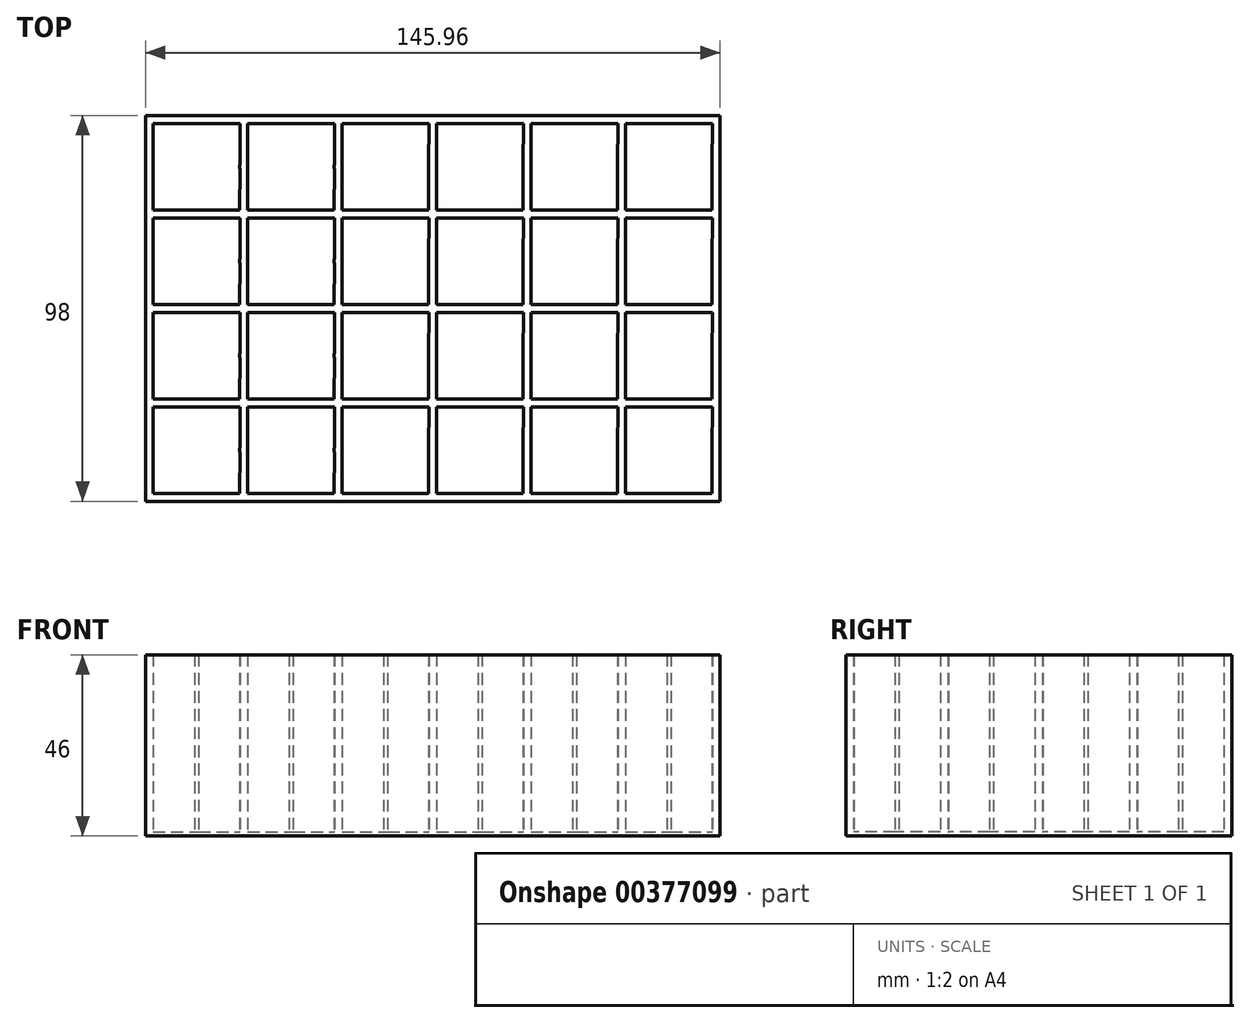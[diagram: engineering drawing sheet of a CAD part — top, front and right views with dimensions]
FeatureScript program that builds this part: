
annotation { "Feature Type Name" : "Feature", "Feature Type Description" : "" }
export const myFeature = defineFeature(function(context is Context, id is Id, definition is map)
    precondition{}
    {
        {
            var Q0;
            Q0=qCreatedBy(makeId("Top.planeOp"),FACE);
            var sketch = newSketch(context, id + "F0", { "sketchPlane" : qUnion([Q0])});
            skLineSegment(sketch, "E0.bottom", {"start": v(-21.96, 22.04) * mm, "end": v(-11.46, 22.02) * mm});
            skLineSegment(sketch, "E0.top", {"start": v(-22, 0.04) * mm, "end": v(-11.46, 0.02) * mm});
            skLineSegment(sketch, "E0.left", {"start": v(-21.96, 22.04) * mm, "end": v(-21.98, 11.54) * mm});
            skLineSegment(sketch, "E0.right", {"start": v(0.04, 22) * mm, "end": v(0.02, 11.54) * mm});
            skLineSegment(sketch, "E1.top", {"start": v(-11.46, 22) * mm, "end": v(-10.46, 22) * mm});
            skLineSegment(sketch, "E1.left", {"start": v(-11.46, 22.02) * mm, "end": v(-11.46, 22) * mm});
            skLineSegment(sketch, "E1.right", {"start": v(-10.46, 22.02) * mm, "end": v(-10.46, 22) * mm});
            skLineSegment(sketch, "E2.bottom", {"start": v(-21.98, 11.54) * mm, "end": v(-21.96, 11.54) * mm});
            skLineSegment(sketch, "E2.top", {"start": v(-21.98, 10.54) * mm, "end": v(-21.96, 10.54) * mm});
            skLineSegment(sketch, "E2.right", {"start": v(-21.96, 11.54) * mm, "end": v(-21.96, 10.54) * mm});
            skLineSegment(sketch, "E3.bottom", {"start": v(0.02, 11.54) * mm, "end": v(0, 11.54) * mm});
            skLineSegment(sketch, "E3.top", {"start": v(0.02, 10.54) * mm, "end": v(0, 10.54) * mm});
            skLineSegment(sketch, "E3.right", {"start": v(0, 11.54) * mm, "end": v(0, 10.54) * mm});
            skLineSegment(sketch, "E4.top", {"start": v(-11.46, 0.04) * mm, "end": v(-10.46, 0.04) * mm});
            skLineSegment(sketch, "E4.left", {"start": v(-11.46, 0.02) * mm, "end": v(-11.46, 0.04) * mm});
            skLineSegment(sketch, "E4.right", {"start": v(-10.46, 0.02) * mm, "end": v(-10.46, 0.04) * mm});
            skLineSegment(sketch, "E5.trimOffspring", {"start": v(-10.46, 22.02) * mm, "end": v(0.04, 22) * mm});
            skLineSegment(sketch, "E6.trimOffspring", {"start": v(-21.98, 10.54) * mm, "end": v(-22, 0.04) * mm});
            skLineSegment(sketch, "E7.trimOffspring", {"start": v(0.02, 10.54) * mm, "end": v(0, 0) * mm});
            skLineSegment(sketch, "E8.trimOffspring", {"start": v(-10.46, 0.02) * mm, "end": v(0, 0) * mm});
            skLineSegment(sketch, "E9.0.1.0", {"start": v(0.04, 46) * mm, "end": v(0.02, 35.54) * mm});
            skLineSegment(sketch, "E9.0.1.1", {"start": v(0.02, 34.54) * mm, "end": v(0, 24) * mm});
            skLineSegment(sketch, "E9.0.1.2", {"start": v(-21.96, 46.04) * mm, "end": v(-21.98, 35.54) * mm});
            skLineSegment(sketch, "E9.0.1.3", {"start": v(-22, 24.04) * mm, "end": v(-11.46, 24.02) * mm});
            skLineSegment(sketch, "E9.0.1.4", {"start": v(-21.96, 46.04) * mm, "end": v(-11.46, 46.02) * mm});
            skLineSegment(sketch, "E9.0.1.5", {"start": v(-10.46, 46.02) * mm, "end": v(0.04, 46) * mm});
            skLineSegment(sketch, "E9.0.1.6", {"start": v(-21.98, 34.54) * mm, "end": v(-22, 24.04) * mm});
            skLineSegment(sketch, "E9.0.1.7", {"start": v(-10.46, 24.02) * mm, "end": v(0, 24) * mm});
            skLineSegment(sketch, "E9.0.1.8", {"start": v(-11.46, 46.02) * mm, "end": v(-11.46, 46) * mm});
            skLineSegment(sketch, "E9.0.1.9", {"start": v(-11.46, 46) * mm, "end": v(-10.46, 46) * mm});
            skLineSegment(sketch, "E9.0.1.10", {"start": v(-10.46, 46.02) * mm, "end": v(-10.46, 46) * mm});
            skLineSegment(sketch, "E9.0.1.11", {"start": v(-21.96, 35.54) * mm, "end": v(-21.96, 34.54) * mm});
            skLineSegment(sketch, "E9.0.1.12", {"start": v(-21.98, 35.54) * mm, "end": v(-21.96, 35.54) * mm});
            skLineSegment(sketch, "E9.0.1.13", {"start": v(-21.98, 34.54) * mm, "end": v(-21.96, 34.54) * mm});
            skLineSegment(sketch, "E9.0.1.14", {"start": v(0.02, 34.54) * mm, "end": v(0, 34.54) * mm});
            skLineSegment(sketch, "E9.0.1.15", {"start": v(0.02, 35.54) * mm, "end": v(0, 35.54) * mm});
            skLineSegment(sketch, "E9.0.1.16", {"start": v(0, 35.54) * mm, "end": v(0, 34.54) * mm});
            skLineSegment(sketch, "E9.0.1.17", {"start": v(-10.46, 24.02) * mm, "end": v(-10.46, 24.04) * mm});
            skLineSegment(sketch, "E9.0.1.18", {"start": v(-11.46, 24.02) * mm, "end": v(-11.46, 24.04) * mm});
            skLineSegment(sketch, "E9.0.1.19", {"start": v(-11.46, 24.04) * mm, "end": v(-10.46, 24.04) * mm});
            skLineSegment(sketch, "E9.0.2.0", {"start": v(0.04, 70) * mm, "end": v(0.02, 59.54) * mm});
            skLineSegment(sketch, "E9.0.2.1", {"start": v(0.02, 58.54) * mm, "end": v(0, 48) * mm});
            skLineSegment(sketch, "E9.0.2.2", {"start": v(-21.96, 70.04) * mm, "end": v(-21.98, 59.54) * mm});
            skLineSegment(sketch, "E9.0.2.3", {"start": v(-22, 48.04) * mm, "end": v(-11.46, 48.02) * mm});
            skLineSegment(sketch, "E9.0.2.4", {"start": v(-21.96, 70.04) * mm, "end": v(-11.46, 70.02) * mm});
            skLineSegment(sketch, "E9.0.2.5", {"start": v(-10.46, 70.02) * mm, "end": v(0.04, 70) * mm});
            skLineSegment(sketch, "E9.0.2.6", {"start": v(-21.98, 58.54) * mm, "end": v(-22, 48.04) * mm});
            skLineSegment(sketch, "E9.0.2.7", {"start": v(-10.46, 48.02) * mm, "end": v(0, 48) * mm});
            skLineSegment(sketch, "E9.0.2.8", {"start": v(-11.46, 70.02) * mm, "end": v(-11.46, 70) * mm});
            skLineSegment(sketch, "E9.0.2.9", {"start": v(-11.46, 70) * mm, "end": v(-10.46, 70) * mm});
            skLineSegment(sketch, "E9.0.2.10", {"start": v(-10.46, 70.02) * mm, "end": v(-10.46, 70) * mm});
            skLineSegment(sketch, "E9.0.2.11", {"start": v(-21.96, 59.54) * mm, "end": v(-21.96, 58.54) * mm});
            skLineSegment(sketch, "E9.0.2.12", {"start": v(-21.98, 59.54) * mm, "end": v(-21.96, 59.54) * mm});
            skLineSegment(sketch, "E9.0.2.13", {"start": v(-21.98, 58.54) * mm, "end": v(-21.96, 58.54) * mm});
            skLineSegment(sketch, "E9.0.2.14", {"start": v(0.02, 58.54) * mm, "end": v(0, 58.54) * mm});
            skLineSegment(sketch, "E9.0.2.15", {"start": v(0.02, 59.54) * mm, "end": v(0, 59.54) * mm});
            skLineSegment(sketch, "E9.0.2.16", {"start": v(0, 59.54) * mm, "end": v(0, 58.54) * mm});
            skLineSegment(sketch, "E9.0.2.17", {"start": v(-10.46, 48.02) * mm, "end": v(-10.46, 48.04) * mm});
            skLineSegment(sketch, "E9.0.2.18", {"start": v(-11.46, 48.02) * mm, "end": v(-11.46, 48.04) * mm});
            skLineSegment(sketch, "E9.0.2.19", {"start": v(-11.46, 48.04) * mm, "end": v(-10.46, 48.04) * mm});
            skLineSegment(sketch, "E9.0.3.0", {"start": v(0.04, 94) * mm, "end": v(0.02, 83.54) * mm});
            skLineSegment(sketch, "E9.0.3.1", {"start": v(0.02, 82.54) * mm, "end": v(0, 72) * mm});
            skLineSegment(sketch, "E9.0.3.2", {"start": v(-21.96, 94.04) * mm, "end": v(-21.98, 83.54) * mm});
            skLineSegment(sketch, "E9.0.3.3", {"start": v(-22, 72.04) * mm, "end": v(-11.46, 72.02) * mm});
            skLineSegment(sketch, "E9.0.3.4", {"start": v(-21.96, 94.04) * mm, "end": v(-11.46, 94.02) * mm});
            skLineSegment(sketch, "E9.0.3.5", {"start": v(-10.46, 94.02) * mm, "end": v(0.04, 94) * mm});
            skLineSegment(sketch, "E9.0.3.6", {"start": v(-21.98, 82.54) * mm, "end": v(-22, 72.04) * mm});
            skLineSegment(sketch, "E9.0.3.7", {"start": v(-10.46, 72.02) * mm, "end": v(0, 72) * mm});
            skLineSegment(sketch, "E9.0.3.8", {"start": v(-11.46, 94.02) * mm, "end": v(-11.46, 94) * mm});
            skLineSegment(sketch, "E9.0.3.9", {"start": v(-11.46, 94) * mm, "end": v(-10.46, 94) * mm});
            skLineSegment(sketch, "E9.0.3.10", {"start": v(-10.46, 94.02) * mm, "end": v(-10.46, 94) * mm});
            skLineSegment(sketch, "E9.0.3.11", {"start": v(-21.96, 83.54) * mm, "end": v(-21.96, 82.54) * mm});
            skLineSegment(sketch, "E9.0.3.12", {"start": v(-21.98, 83.54) * mm, "end": v(-21.96, 83.54) * mm});
            skLineSegment(sketch, "E9.0.3.13", {"start": v(-21.98, 82.54) * mm, "end": v(-21.96, 82.54) * mm});
            skLineSegment(sketch, "E9.0.3.14", {"start": v(0.02, 82.54) * mm, "end": v(0, 82.54) * mm});
            skLineSegment(sketch, "E9.0.3.15", {"start": v(0.02, 83.54) * mm, "end": v(0, 83.54) * mm});
            skLineSegment(sketch, "E9.0.3.16", {"start": v(0, 83.54) * mm, "end": v(0, 82.54) * mm});
            skLineSegment(sketch, "E9.0.3.17", {"start": v(-10.46, 72.02) * mm, "end": v(-10.46, 72.04) * mm});
            skLineSegment(sketch, "E9.0.3.18", {"start": v(-11.46, 72.02) * mm, "end": v(-11.46, 72.04) * mm});
            skLineSegment(sketch, "E9.0.3.19", {"start": v(-11.46, 72.04) * mm, "end": v(-10.46, 72.04) * mm});
            skLineSegment(sketch, "E9.1.0.0", {"start": v(24.04, 22) * mm, "end": v(24.02, 11.54) * mm});
            skLineSegment(sketch, "E9.1.0.1", {"start": v(24.02, 10.54) * mm, "end": v(24, 0) * mm});
            skLineSegment(sketch, "E9.1.0.2", {"start": v(2.04, 22.04) * mm, "end": v(2.02, 11.54) * mm});
            skLineSegment(sketch, "E9.1.0.3", {"start": v(2, 0.04) * mm, "end": v(12.54, 0.02) * mm});
            skLineSegment(sketch, "E9.1.0.4", {"start": v(2.04, 22.04) * mm, "end": v(12.54, 22.02) * mm});
            skLineSegment(sketch, "E9.1.0.5", {"start": v(13.54, 22.02) * mm, "end": v(24.04, 22) * mm});
            skLineSegment(sketch, "E9.1.0.6", {"start": v(2.02, 10.54) * mm, "end": v(2, 0.04) * mm});
            skLineSegment(sketch, "E9.1.0.7", {"start": v(13.54, 0.02) * mm, "end": v(24, 0) * mm});
            skLineSegment(sketch, "E9.1.0.8", {"start": v(12.54, 22.02) * mm, "end": v(12.54, 22) * mm});
            skLineSegment(sketch, "E9.1.0.9", {"start": v(12.54, 22) * mm, "end": v(13.54, 22) * mm});
            skLineSegment(sketch, "E9.1.0.10", {"start": v(13.54, 22.02) * mm, "end": v(13.54, 22) * mm});
            skLineSegment(sketch, "E9.1.0.11", {"start": v(2.04, 11.54) * mm, "end": v(2.04, 10.54) * mm});
            skLineSegment(sketch, "E9.1.0.12", {"start": v(2.02, 11.54) * mm, "end": v(2.04, 11.54) * mm});
            skLineSegment(sketch, "E9.1.0.13", {"start": v(2.02, 10.54) * mm, "end": v(2.04, 10.54) * mm});
            skLineSegment(sketch, "E9.1.0.14", {"start": v(24.02, 10.54) * mm, "end": v(24, 10.54) * mm});
            skLineSegment(sketch, "E9.1.0.15", {"start": v(24.02, 11.54) * mm, "end": v(24, 11.54) * mm});
            skLineSegment(sketch, "E9.1.0.16", {"start": v(24, 11.54) * mm, "end": v(24, 10.54) * mm});
            skLineSegment(sketch, "E9.1.0.17", {"start": v(13.54, 0.02) * mm, "end": v(13.54, 0.04) * mm});
            skLineSegment(sketch, "E9.1.0.18", {"start": v(12.54, 0.02) * mm, "end": v(12.54, 0.04) * mm});
            skLineSegment(sketch, "E9.1.0.19", {"start": v(12.54, 0.04) * mm, "end": v(13.54, 0.04) * mm});
            skLineSegment(sketch, "E9.1.1.0", {"start": v(24.04, 46) * mm, "end": v(24.02, 35.54) * mm});
            skLineSegment(sketch, "E9.1.1.1", {"start": v(24.02, 34.54) * mm, "end": v(24, 24) * mm});
            skLineSegment(sketch, "E9.1.1.2", {"start": v(2.04, 46.04) * mm, "end": v(2.02, 35.54) * mm});
            skLineSegment(sketch, "E9.1.1.3", {"start": v(2, 24.04) * mm, "end": v(12.54, 24.02) * mm});
            skLineSegment(sketch, "E9.1.1.4", {"start": v(2.04, 46.04) * mm, "end": v(12.54, 46.02) * mm});
            skLineSegment(sketch, "E9.1.1.5", {"start": v(13.54, 46.02) * mm, "end": v(24.04, 46) * mm});
            skLineSegment(sketch, "E9.1.1.6", {"start": v(2.02, 34.54) * mm, "end": v(2, 24.04) * mm});
            skLineSegment(sketch, "E9.1.1.7", {"start": v(13.54, 24.02) * mm, "end": v(24, 24) * mm});
            skLineSegment(sketch, "E9.1.1.8", {"start": v(12.54, 46.02) * mm, "end": v(12.54, 46) * mm});
            skLineSegment(sketch, "E9.1.1.9", {"start": v(12.54, 46) * mm, "end": v(13.54, 46) * mm});
            skLineSegment(sketch, "E9.1.1.10", {"start": v(13.54, 46.02) * mm, "end": v(13.54, 46) * mm});
            skLineSegment(sketch, "E9.1.1.11", {"start": v(2.04, 35.54) * mm, "end": v(2.04, 34.54) * mm});
            skLineSegment(sketch, "E9.1.1.12", {"start": v(2.02, 35.54) * mm, "end": v(2.04, 35.54) * mm});
            skLineSegment(sketch, "E9.1.1.13", {"start": v(2.02, 34.54) * mm, "end": v(2.04, 34.54) * mm});
            skLineSegment(sketch, "E9.1.1.14", {"start": v(24.02, 34.54) * mm, "end": v(24, 34.54) * mm});
            skLineSegment(sketch, "E9.1.1.15", {"start": v(24.02, 35.54) * mm, "end": v(24, 35.54) * mm});
            skLineSegment(sketch, "E9.1.1.16", {"start": v(24, 35.54) * mm, "end": v(24, 34.54) * mm});
            skLineSegment(sketch, "E9.1.1.17", {"start": v(13.54, 24.02) * mm, "end": v(13.54, 24.04) * mm});
            skLineSegment(sketch, "E9.1.1.18", {"start": v(12.54, 24.02) * mm, "end": v(12.54, 24.04) * mm});
            skLineSegment(sketch, "E9.1.1.19", {"start": v(12.54, 24.04) * mm, "end": v(13.54, 24.04) * mm});
            skLineSegment(sketch, "E9.1.2.0", {"start": v(24.04, 70) * mm, "end": v(24.02, 59.54) * mm});
            skLineSegment(sketch, "E9.1.2.1", {"start": v(24.02, 58.54) * mm, "end": v(24, 48) * mm});
            skLineSegment(sketch, "E9.1.2.2", {"start": v(2.04, 70.04) * mm, "end": v(2.02, 59.54) * mm});
            skLineSegment(sketch, "E9.1.2.3", {"start": v(2, 48.04) * mm, "end": v(12.54, 48.02) * mm});
            skLineSegment(sketch, "E9.1.2.4", {"start": v(2.04, 70.04) * mm, "end": v(12.54, 70.02) * mm});
            skLineSegment(sketch, "E9.1.2.5", {"start": v(13.54, 70.02) * mm, "end": v(24.04, 70) * mm});
            skLineSegment(sketch, "E9.1.2.6", {"start": v(2.02, 58.54) * mm, "end": v(2, 48.04) * mm});
            skLineSegment(sketch, "E9.1.2.7", {"start": v(13.54, 48.02) * mm, "end": v(24, 48) * mm});
            skLineSegment(sketch, "E9.1.2.8", {"start": v(12.54, 70.02) * mm, "end": v(12.54, 70) * mm});
            skLineSegment(sketch, "E9.1.2.9", {"start": v(12.54, 70) * mm, "end": v(13.54, 70) * mm});
            skLineSegment(sketch, "E9.1.2.10", {"start": v(13.54, 70.02) * mm, "end": v(13.54, 70) * mm});
            skLineSegment(sketch, "E9.1.2.11", {"start": v(2.04, 59.54) * mm, "end": v(2.04, 58.54) * mm});
            skLineSegment(sketch, "E9.1.2.12", {"start": v(2.02, 59.54) * mm, "end": v(2.04, 59.54) * mm});
            skLineSegment(sketch, "E9.1.2.13", {"start": v(2.02, 58.54) * mm, "end": v(2.04, 58.54) * mm});
            skLineSegment(sketch, "E9.1.2.14", {"start": v(24.02, 58.54) * mm, "end": v(24, 58.54) * mm});
            skLineSegment(sketch, "E9.1.2.15", {"start": v(24.02, 59.54) * mm, "end": v(24, 59.54) * mm});
            skLineSegment(sketch, "E9.1.2.16", {"start": v(24, 59.54) * mm, "end": v(24, 58.54) * mm});
            skLineSegment(sketch, "E9.1.2.17", {"start": v(13.54, 48.02) * mm, "end": v(13.54, 48.04) * mm});
            skLineSegment(sketch, "E9.1.2.18", {"start": v(12.54, 48.02) * mm, "end": v(12.54, 48.04) * mm});
            skLineSegment(sketch, "E9.1.2.19", {"start": v(12.54, 48.04) * mm, "end": v(13.54, 48.04) * mm});
            skLineSegment(sketch, "E9.1.3.0", {"start": v(24.04, 94) * mm, "end": v(24.02, 83.54) * mm});
            skLineSegment(sketch, "E9.1.3.1", {"start": v(24.02, 82.54) * mm, "end": v(24, 72) * mm});
            skLineSegment(sketch, "E9.1.3.2", {"start": v(2.04, 94.04) * mm, "end": v(2.02, 83.54) * mm});
            skLineSegment(sketch, "E9.1.3.3", {"start": v(2, 72.04) * mm, "end": v(12.54, 72.02) * mm});
            skLineSegment(sketch, "E9.1.3.4", {"start": v(2.04, 94.04) * mm, "end": v(12.54, 94.02) * mm});
            skLineSegment(sketch, "E9.1.3.5", {"start": v(13.54, 94.02) * mm, "end": v(24.04, 94) * mm});
            skLineSegment(sketch, "E9.1.3.6", {"start": v(2.02, 82.54) * mm, "end": v(2, 72.04) * mm});
            skLineSegment(sketch, "E9.1.3.7", {"start": v(13.54, 72.02) * mm, "end": v(24, 72) * mm});
            skLineSegment(sketch, "E9.1.3.8", {"start": v(12.54, 94.02) * mm, "end": v(12.54, 94) * mm});
            skLineSegment(sketch, "E9.1.3.9", {"start": v(12.54, 94) * mm, "end": v(13.54, 94) * mm});
            skLineSegment(sketch, "E9.1.3.10", {"start": v(13.54, 94.02) * mm, "end": v(13.54, 94) * mm});
            skLineSegment(sketch, "E9.1.3.11", {"start": v(2.04, 83.54) * mm, "end": v(2.04, 82.54) * mm});
            skLineSegment(sketch, "E9.1.3.12", {"start": v(2.02, 83.54) * mm, "end": v(2.04, 83.54) * mm});
            skLineSegment(sketch, "E9.1.3.13", {"start": v(2.02, 82.54) * mm, "end": v(2.04, 82.54) * mm});
            skLineSegment(sketch, "E9.1.3.14", {"start": v(24.02, 82.54) * mm, "end": v(24, 82.54) * mm});
            skLineSegment(sketch, "E9.1.3.15", {"start": v(24.02, 83.54) * mm, "end": v(24, 83.54) * mm});
            skLineSegment(sketch, "E9.1.3.16", {"start": v(24, 83.54) * mm, "end": v(24, 82.54) * mm});
            skLineSegment(sketch, "E9.1.3.17", {"start": v(13.54, 72.02) * mm, "end": v(13.54, 72.04) * mm});
            skLineSegment(sketch, "E9.1.3.18", {"start": v(12.54, 72.02) * mm, "end": v(12.54, 72.04) * mm});
            skLineSegment(sketch, "E9.1.3.19", {"start": v(12.54, 72.04) * mm, "end": v(13.54, 72.04) * mm});
            skLineSegment(sketch, "E9.2.0.0", {"start": v(48.04, 22) * mm, "end": v(48.02, 11.54) * mm});
            skLineSegment(sketch, "E9.2.0.1", {"start": v(48.02, 10.54) * mm, "end": v(48, 0) * mm});
            skLineSegment(sketch, "E9.2.0.2", {"start": v(26.04, 22.04) * mm, "end": v(26.02, 11.54) * mm});
            skLineSegment(sketch, "E9.2.0.3", {"start": v(26, 0.04) * mm, "end": v(36.54, 0.02) * mm});
            skLineSegment(sketch, "E9.2.0.4", {"start": v(26.04, 22.04) * mm, "end": v(36.54, 22.02) * mm});
            skLineSegment(sketch, "E9.2.0.5", {"start": v(37.54, 22.02) * mm, "end": v(48.04, 22) * mm});
            skLineSegment(sketch, "E9.2.0.6", {"start": v(26.02, 10.54) * mm, "end": v(26, 0.04) * mm});
            skLineSegment(sketch, "E9.2.0.7", {"start": v(37.54, 0.02) * mm, "end": v(48, 0) * mm});
            skLineSegment(sketch, "E9.2.0.8", {"start": v(36.54, 22.02) * mm, "end": v(36.54, 22) * mm});
            skLineSegment(sketch, "E9.2.0.9", {"start": v(36.54, 22) * mm, "end": v(37.54, 22) * mm});
            skLineSegment(sketch, "E9.2.0.10", {"start": v(37.54, 22.02) * mm, "end": v(37.54, 22) * mm});
            skLineSegment(sketch, "E9.2.0.11", {"start": v(26.04, 11.54) * mm, "end": v(26.04, 10.54) * mm});
            skLineSegment(sketch, "E9.2.0.12", {"start": v(26.02, 11.54) * mm, "end": v(26.04, 11.54) * mm});
            skLineSegment(sketch, "E9.2.0.13", {"start": v(26.02, 10.54) * mm, "end": v(26.04, 10.54) * mm});
            skLineSegment(sketch, "E9.2.0.14", {"start": v(48.02, 10.54) * mm, "end": v(48, 10.54) * mm});
            skLineSegment(sketch, "E9.2.0.15", {"start": v(48.02, 11.54) * mm, "end": v(48, 11.54) * mm});
            skLineSegment(sketch, "E9.2.0.16", {"start": v(48, 11.54) * mm, "end": v(48, 10.54) * mm});
            skLineSegment(sketch, "E9.2.0.17", {"start": v(37.54, 0.02) * mm, "end": v(37.54, 0.04) * mm});
            skLineSegment(sketch, "E9.2.0.18", {"start": v(36.54, 0.02) * mm, "end": v(36.54, 0.04) * mm});
            skLineSegment(sketch, "E9.2.0.19", {"start": v(36.54, 0.04) * mm, "end": v(37.54, 0.04) * mm});
            skLineSegment(sketch, "E9.2.1.0", {"start": v(48.04, 46) * mm, "end": v(48.02, 35.54) * mm});
            skLineSegment(sketch, "E9.2.1.1", {"start": v(48.02, 34.54) * mm, "end": v(48, 24) * mm});
            skLineSegment(sketch, "E9.2.1.2", {"start": v(26.04, 46.04) * mm, "end": v(26.02, 35.54) * mm});
            skLineSegment(sketch, "E9.2.1.3", {"start": v(26, 24.04) * mm, "end": v(36.54, 24.02) * mm});
            skLineSegment(sketch, "E9.2.1.4", {"start": v(26.04, 46.04) * mm, "end": v(36.54, 46.02) * mm});
            skLineSegment(sketch, "E9.2.1.5", {"start": v(37.54, 46.02) * mm, "end": v(48.04, 46) * mm});
            skLineSegment(sketch, "E9.2.1.6", {"start": v(26.02, 34.54) * mm, "end": v(26, 24.04) * mm});
            skLineSegment(sketch, "E9.2.1.7", {"start": v(37.54, 24.02) * mm, "end": v(48, 24) * mm});
            skLineSegment(sketch, "E9.2.1.8", {"start": v(36.54, 46.02) * mm, "end": v(36.54, 46) * mm});
            skLineSegment(sketch, "E9.2.1.9", {"start": v(36.54, 46) * mm, "end": v(37.54, 46) * mm});
            skLineSegment(sketch, "E9.2.1.10", {"start": v(37.54, 46.02) * mm, "end": v(37.54, 46) * mm});
            skLineSegment(sketch, "E9.2.1.11", {"start": v(26.04, 35.54) * mm, "end": v(26.04, 34.54) * mm});
            skLineSegment(sketch, "E9.2.1.12", {"start": v(26.02, 35.54) * mm, "end": v(26.04, 35.54) * mm});
            skLineSegment(sketch, "E9.2.1.13", {"start": v(26.02, 34.54) * mm, "end": v(26.04, 34.54) * mm});
            skLineSegment(sketch, "E9.2.1.14", {"start": v(48.02, 34.54) * mm, "end": v(48, 34.54) * mm});
            skLineSegment(sketch, "E9.2.1.15", {"start": v(48.02, 35.54) * mm, "end": v(48, 35.54) * mm});
            skLineSegment(sketch, "E9.2.1.16", {"start": v(48, 35.54) * mm, "end": v(48, 34.54) * mm});
            skLineSegment(sketch, "E9.2.1.17", {"start": v(37.54, 24.02) * mm, "end": v(37.54, 24.04) * mm});
            skLineSegment(sketch, "E9.2.1.18", {"start": v(36.54, 24.02) * mm, "end": v(36.54, 24.04) * mm});
            skLineSegment(sketch, "E9.2.1.19", {"start": v(36.54, 24.04) * mm, "end": v(37.54, 24.04) * mm});
            skLineSegment(sketch, "E9.2.2.0", {"start": v(48.04, 70) * mm, "end": v(48.02, 59.54) * mm});
            skLineSegment(sketch, "E9.2.2.1", {"start": v(48.02, 58.54) * mm, "end": v(48, 48) * mm});
            skLineSegment(sketch, "E9.2.2.2", {"start": v(26.04, 70.04) * mm, "end": v(26.02, 59.54) * mm});
            skLineSegment(sketch, "E9.2.2.3", {"start": v(26, 48.04) * mm, "end": v(36.54, 48.02) * mm});
            skLineSegment(sketch, "E9.2.2.4", {"start": v(26.04, 70.04) * mm, "end": v(36.54, 70.02) * mm});
            skLineSegment(sketch, "E9.2.2.5", {"start": v(37.54, 70.02) * mm, "end": v(48.04, 70) * mm});
            skLineSegment(sketch, "E9.2.2.6", {"start": v(26.02, 58.54) * mm, "end": v(26, 48.04) * mm});
            skLineSegment(sketch, "E9.2.2.7", {"start": v(37.54, 48.02) * mm, "end": v(48, 48) * mm});
            skLineSegment(sketch, "E9.2.2.8", {"start": v(36.54, 70.02) * mm, "end": v(36.54, 70) * mm});
            skLineSegment(sketch, "E9.2.2.9", {"start": v(36.54, 70) * mm, "end": v(37.54, 70) * mm});
            skLineSegment(sketch, "E9.2.2.10", {"start": v(37.54, 70.02) * mm, "end": v(37.54, 70) * mm});
            skLineSegment(sketch, "E9.2.2.11", {"start": v(26.04, 59.54) * mm, "end": v(26.04, 58.54) * mm});
            skLineSegment(sketch, "E9.2.2.12", {"start": v(26.02, 59.54) * mm, "end": v(26.04, 59.54) * mm});
            skLineSegment(sketch, "E9.2.2.13", {"start": v(26.02, 58.54) * mm, "end": v(26.04, 58.54) * mm});
            skLineSegment(sketch, "E9.2.2.14", {"start": v(48.02, 58.54) * mm, "end": v(48, 58.54) * mm});
            skLineSegment(sketch, "E9.2.2.15", {"start": v(48.02, 59.54) * mm, "end": v(48, 59.54) * mm});
            skLineSegment(sketch, "E9.2.2.16", {"start": v(48, 59.54) * mm, "end": v(48, 58.54) * mm});
            skLineSegment(sketch, "E9.2.2.17", {"start": v(37.54, 48.02) * mm, "end": v(37.54, 48.04) * mm});
            skLineSegment(sketch, "E9.2.2.18", {"start": v(36.54, 48.02) * mm, "end": v(36.54, 48.04) * mm});
            skLineSegment(sketch, "E9.2.2.19", {"start": v(36.54, 48.04) * mm, "end": v(37.54, 48.04) * mm});
            skLineSegment(sketch, "E9.2.3.0", {"start": v(48.04, 94) * mm, "end": v(48.02, 83.54) * mm});
            skLineSegment(sketch, "E9.2.3.1", {"start": v(48.02, 82.54) * mm, "end": v(48, 72) * mm});
            skLineSegment(sketch, "E9.2.3.2", {"start": v(26.04, 94.04) * mm, "end": v(26.02, 83.54) * mm});
            skLineSegment(sketch, "E9.2.3.3", {"start": v(26, 72.04) * mm, "end": v(36.54, 72.02) * mm});
            skLineSegment(sketch, "E9.2.3.4", {"start": v(26.04, 94.04) * mm, "end": v(36.54, 94.02) * mm});
            skLineSegment(sketch, "E9.2.3.5", {"start": v(37.54, 94.02) * mm, "end": v(48.04, 94) * mm});
            skLineSegment(sketch, "E9.2.3.6", {"start": v(26.02, 82.54) * mm, "end": v(26, 72.04) * mm});
            skLineSegment(sketch, "E9.2.3.7", {"start": v(37.54, 72.02) * mm, "end": v(48, 72) * mm});
            skLineSegment(sketch, "E9.2.3.8", {"start": v(36.54, 94.02) * mm, "end": v(36.54, 94) * mm});
            skLineSegment(sketch, "E9.2.3.9", {"start": v(36.54, 94) * mm, "end": v(37.54, 94) * mm});
            skLineSegment(sketch, "E9.2.3.10", {"start": v(37.54, 94.02) * mm, "end": v(37.54, 94) * mm});
            skLineSegment(sketch, "E9.2.3.11", {"start": v(26.04, 83.54) * mm, "end": v(26.04, 82.54) * mm});
            skLineSegment(sketch, "E9.2.3.12", {"start": v(26.02, 83.54) * mm, "end": v(26.04, 83.54) * mm});
            skLineSegment(sketch, "E9.2.3.13", {"start": v(26.02, 82.54) * mm, "end": v(26.04, 82.54) * mm});
            skLineSegment(sketch, "E9.2.3.14", {"start": v(48.02, 82.54) * mm, "end": v(48, 82.54) * mm});
            skLineSegment(sketch, "E9.2.3.15", {"start": v(48.02, 83.54) * mm, "end": v(48, 83.54) * mm});
            skLineSegment(sketch, "E9.2.3.16", {"start": v(48, 83.54) * mm, "end": v(48, 82.54) * mm});
            skLineSegment(sketch, "E9.2.3.17", {"start": v(37.54, 72.02) * mm, "end": v(37.54, 72.04) * mm});
            skLineSegment(sketch, "E9.2.3.18", {"start": v(36.54, 72.02) * mm, "end": v(36.54, 72.04) * mm});
            skLineSegment(sketch, "E9.2.3.19", {"start": v(36.54, 72.04) * mm, "end": v(37.54, 72.04) * mm});
            skLineSegment(sketch, "E9.3.0.0", {"start": v(72.04, 22) * mm, "end": v(72.02, 11.54) * mm});
            skLineSegment(sketch, "E9.3.0.1", {"start": v(72.02, 10.54) * mm, "end": v(72, 0) * mm});
            skLineSegment(sketch, "E9.3.0.2", {"start": v(50.04, 22.04) * mm, "end": v(50.02, 11.54) * mm});
            skLineSegment(sketch, "E9.3.0.3", {"start": v(50, 0.04) * mm, "end": v(60.54, 0.02) * mm});
            skLineSegment(sketch, "E9.3.0.4", {"start": v(50.04, 22.04) * mm, "end": v(60.54, 22.02) * mm});
            skLineSegment(sketch, "E9.3.0.5", {"start": v(61.54, 22.02) * mm, "end": v(72.04, 22) * mm});
            skLineSegment(sketch, "E9.3.0.6", {"start": v(50.02, 10.54) * mm, "end": v(50, 0.04) * mm});
            skLineSegment(sketch, "E9.3.0.7", {"start": v(61.54, 0.02) * mm, "end": v(72, 0) * mm});
            skLineSegment(sketch, "E9.3.0.8", {"start": v(60.54, 22.02) * mm, "end": v(60.54, 22) * mm});
            skLineSegment(sketch, "E9.3.0.9", {"start": v(60.54, 22) * mm, "end": v(61.54, 22) * mm});
            skLineSegment(sketch, "E9.3.0.10", {"start": v(61.54, 22.02) * mm, "end": v(61.54, 22) * mm});
            skLineSegment(sketch, "E9.3.0.11", {"start": v(50.04, 11.54) * mm, "end": v(50.04, 10.54) * mm});
            skLineSegment(sketch, "E9.3.0.12", {"start": v(50.02, 11.54) * mm, "end": v(50.04, 11.54) * mm});
            skLineSegment(sketch, "E9.3.0.13", {"start": v(50.02, 10.54) * mm, "end": v(50.04, 10.54) * mm});
            skLineSegment(sketch, "E9.3.0.14", {"start": v(72.02, 10.54) * mm, "end": v(72, 10.54) * mm});
            skLineSegment(sketch, "E9.3.0.15", {"start": v(72.02, 11.54) * mm, "end": v(72, 11.54) * mm});
            skLineSegment(sketch, "E9.3.0.16", {"start": v(72, 11.54) * mm, "end": v(72, 10.54) * mm});
            skLineSegment(sketch, "E9.3.0.17", {"start": v(61.54, 0.02) * mm, "end": v(61.54, 0.04) * mm});
            skLineSegment(sketch, "E9.3.0.18", {"start": v(60.54, 0.02) * mm, "end": v(60.54, 0.04) * mm});
            skLineSegment(sketch, "E9.3.0.19", {"start": v(60.54, 0.04) * mm, "end": v(61.54, 0.04) * mm});
            skLineSegment(sketch, "E9.3.1.0", {"start": v(72.04, 46) * mm, "end": v(72.02, 35.54) * mm});
            skLineSegment(sketch, "E9.3.1.1", {"start": v(72.02, 34.54) * mm, "end": v(72, 24) * mm});
            skLineSegment(sketch, "E9.3.1.2", {"start": v(50.04, 46.04) * mm, "end": v(50.02, 35.54) * mm});
            skLineSegment(sketch, "E9.3.1.3", {"start": v(50, 24.04) * mm, "end": v(60.54, 24.02) * mm});
            skLineSegment(sketch, "E9.3.1.4", {"start": v(50.04, 46.04) * mm, "end": v(60.54, 46.02) * mm});
            skLineSegment(sketch, "E9.3.1.5", {"start": v(61.54, 46.02) * mm, "end": v(72.04, 46) * mm});
            skLineSegment(sketch, "E9.3.1.6", {"start": v(50.02, 34.54) * mm, "end": v(50, 24.04) * mm});
            skLineSegment(sketch, "E9.3.1.7", {"start": v(61.54, 24.02) * mm, "end": v(72, 24) * mm});
            skLineSegment(sketch, "E9.3.1.8", {"start": v(60.54, 46.02) * mm, "end": v(60.54, 46) * mm});
            skLineSegment(sketch, "E9.3.1.9", {"start": v(60.54, 46) * mm, "end": v(61.54, 46) * mm});
            skLineSegment(sketch, "E9.3.1.10", {"start": v(61.54, 46.02) * mm, "end": v(61.54, 46) * mm});
            skLineSegment(sketch, "E9.3.1.11", {"start": v(50.04, 35.54) * mm, "end": v(50.04, 34.54) * mm});
            skLineSegment(sketch, "E9.3.1.12", {"start": v(50.02, 35.54) * mm, "end": v(50.04, 35.54) * mm});
            skLineSegment(sketch, "E9.3.1.13", {"start": v(50.02, 34.54) * mm, "end": v(50.04, 34.54) * mm});
            skLineSegment(sketch, "E9.3.1.14", {"start": v(72.02, 34.54) * mm, "end": v(72, 34.54) * mm});
            skLineSegment(sketch, "E9.3.1.15", {"start": v(72.02, 35.54) * mm, "end": v(72, 35.54) * mm});
            skLineSegment(sketch, "E9.3.1.16", {"start": v(72, 35.54) * mm, "end": v(72, 34.54) * mm});
            skLineSegment(sketch, "E9.3.1.17", {"start": v(61.54, 24.02) * mm, "end": v(61.54, 24.04) * mm});
            skLineSegment(sketch, "E9.3.1.18", {"start": v(60.54, 24.02) * mm, "end": v(60.54, 24.04) * mm});
            skLineSegment(sketch, "E9.3.1.19", {"start": v(60.54, 24.04) * mm, "end": v(61.54, 24.04) * mm});
            skLineSegment(sketch, "E9.3.2.0", {"start": v(72.04, 70) * mm, "end": v(72.02, 59.54) * mm});
            skLineSegment(sketch, "E9.3.2.1", {"start": v(72.02, 58.54) * mm, "end": v(72, 48) * mm});
            skLineSegment(sketch, "E9.3.2.2", {"start": v(50.04, 70.04) * mm, "end": v(50.02, 59.54) * mm});
            skLineSegment(sketch, "E9.3.2.3", {"start": v(50, 48.04) * mm, "end": v(60.54, 48.02) * mm});
            skLineSegment(sketch, "E9.3.2.4", {"start": v(50.04, 70.04) * mm, "end": v(60.54, 70.02) * mm});
            skLineSegment(sketch, "E9.3.2.5", {"start": v(61.54, 70.02) * mm, "end": v(72.04, 70) * mm});
            skLineSegment(sketch, "E9.3.2.6", {"start": v(50.02, 58.54) * mm, "end": v(50, 48.04) * mm});
            skLineSegment(sketch, "E9.3.2.7", {"start": v(61.54, 48.02) * mm, "end": v(72, 48) * mm});
            skLineSegment(sketch, "E9.3.2.8", {"start": v(60.54, 70.02) * mm, "end": v(60.54, 70) * mm});
            skLineSegment(sketch, "E9.3.2.9", {"start": v(60.54, 70) * mm, "end": v(61.54, 70) * mm});
            skLineSegment(sketch, "E9.3.2.10", {"start": v(61.54, 70.02) * mm, "end": v(61.54, 70) * mm});
            skLineSegment(sketch, "E9.3.2.11", {"start": v(50.04, 59.54) * mm, "end": v(50.04, 58.54) * mm});
            skLineSegment(sketch, "E9.3.2.12", {"start": v(50.02, 59.54) * mm, "end": v(50.04, 59.54) * mm});
            skLineSegment(sketch, "E9.3.2.13", {"start": v(50.02, 58.54) * mm, "end": v(50.04, 58.54) * mm});
            skLineSegment(sketch, "E9.3.2.14", {"start": v(72.02, 58.54) * mm, "end": v(72, 58.54) * mm});
            skLineSegment(sketch, "E9.3.2.15", {"start": v(72.02, 59.54) * mm, "end": v(72, 59.54) * mm});
            skLineSegment(sketch, "E9.3.2.16", {"start": v(72, 59.54) * mm, "end": v(72, 58.54) * mm});
            skLineSegment(sketch, "E9.3.2.17", {"start": v(61.54, 48.02) * mm, "end": v(61.54, 48.04) * mm});
            skLineSegment(sketch, "E9.3.2.18", {"start": v(60.54, 48.02) * mm, "end": v(60.54, 48.04) * mm});
            skLineSegment(sketch, "E9.3.2.19", {"start": v(60.54, 48.04) * mm, "end": v(61.54, 48.04) * mm});
            skLineSegment(sketch, "E9.3.3.0", {"start": v(72.04, 94) * mm, "end": v(72.02, 83.54) * mm});
            skLineSegment(sketch, "E9.3.3.1", {"start": v(72.02, 82.54) * mm, "end": v(72, 72) * mm});
            skLineSegment(sketch, "E9.3.3.2", {"start": v(50.04, 94.04) * mm, "end": v(50.02, 83.54) * mm});
            skLineSegment(sketch, "E9.3.3.3", {"start": v(50, 72.04) * mm, "end": v(60.54, 72.02) * mm});
            skLineSegment(sketch, "E9.3.3.4", {"start": v(50.04, 94.04) * mm, "end": v(60.54, 94.02) * mm});
            skLineSegment(sketch, "E9.3.3.5", {"start": v(61.54, 94.02) * mm, "end": v(72.04, 94) * mm});
            skLineSegment(sketch, "E9.3.3.6", {"start": v(50.02, 82.54) * mm, "end": v(50, 72.04) * mm});
            skLineSegment(sketch, "E9.3.3.7", {"start": v(61.54, 72.02) * mm, "end": v(72, 72) * mm});
            skLineSegment(sketch, "E9.3.3.8", {"start": v(60.54, 94.02) * mm, "end": v(60.54, 94) * mm});
            skLineSegment(sketch, "E9.3.3.9", {"start": v(60.54, 94) * mm, "end": v(61.54, 94) * mm});
            skLineSegment(sketch, "E9.3.3.10", {"start": v(61.54, 94.02) * mm, "end": v(61.54, 94) * mm});
            skLineSegment(sketch, "E9.3.3.11", {"start": v(50.04, 83.54) * mm, "end": v(50.04, 82.54) * mm});
            skLineSegment(sketch, "E9.3.3.12", {"start": v(50.02, 83.54) * mm, "end": v(50.04, 83.54) * mm});
            skLineSegment(sketch, "E9.3.3.13", {"start": v(50.02, 82.54) * mm, "end": v(50.04, 82.54) * mm});
            skLineSegment(sketch, "E9.3.3.14", {"start": v(72.02, 82.54) * mm, "end": v(72, 82.54) * mm});
            skLineSegment(sketch, "E9.3.3.15", {"start": v(72.02, 83.54) * mm, "end": v(72, 83.54) * mm});
            skLineSegment(sketch, "E9.3.3.16", {"start": v(72, 83.54) * mm, "end": v(72, 82.54) * mm});
            skLineSegment(sketch, "E9.3.3.17", {"start": v(61.54, 72.02) * mm, "end": v(61.54, 72.04) * mm});
            skLineSegment(sketch, "E9.3.3.18", {"start": v(60.54, 72.02) * mm, "end": v(60.54, 72.04) * mm});
            skLineSegment(sketch, "E9.3.3.19", {"start": v(60.54, 72.04) * mm, "end": v(61.54, 72.04) * mm});
            skLineSegment(sketch, "E9.4.0.0", {"start": v(96.04, 22) * mm, "end": v(96.02, 11.54) * mm});
            skLineSegment(sketch, "E9.4.0.1", {"start": v(96.02, 10.54) * mm, "end": v(96, 0) * mm});
            skLineSegment(sketch, "E9.4.0.2", {"start": v(74.04, 22.04) * mm, "end": v(74.02, 11.54) * mm});
            skLineSegment(sketch, "E9.4.0.3", {"start": v(74, 0.04) * mm, "end": v(84.54, 0.02) * mm});
            skLineSegment(sketch, "E9.4.0.4", {"start": v(74.04, 22.04) * mm, "end": v(84.54, 22.02) * mm});
            skLineSegment(sketch, "E9.4.0.5", {"start": v(85.54, 22.02) * mm, "end": v(96.04, 22) * mm});
            skLineSegment(sketch, "E9.4.0.6", {"start": v(74.02, 10.54) * mm, "end": v(74, 0.04) * mm});
            skLineSegment(sketch, "E9.4.0.7", {"start": v(85.54, 0.02) * mm, "end": v(96, 0) * mm});
            skLineSegment(sketch, "E9.4.0.8", {"start": v(84.54, 22.02) * mm, "end": v(84.54, 22) * mm});
            skLineSegment(sketch, "E9.4.0.9", {"start": v(84.54, 22) * mm, "end": v(85.54, 22) * mm});
            skLineSegment(sketch, "E9.4.0.10", {"start": v(85.54, 22.02) * mm, "end": v(85.54, 22) * mm});
            skLineSegment(sketch, "E9.4.0.11", {"start": v(74.04, 11.54) * mm, "end": v(74.04, 10.54) * mm});
            skLineSegment(sketch, "E9.4.0.12", {"start": v(74.02, 11.54) * mm, "end": v(74.04, 11.54) * mm});
            skLineSegment(sketch, "E9.4.0.13", {"start": v(74.02, 10.54) * mm, "end": v(74.04, 10.54) * mm});
            skLineSegment(sketch, "E9.4.0.14", {"start": v(96.02, 10.54) * mm, "end": v(96, 10.54) * mm});
            skLineSegment(sketch, "E9.4.0.15", {"start": v(96.02, 11.54) * mm, "end": v(96, 11.54) * mm});
            skLineSegment(sketch, "E9.4.0.16", {"start": v(96, 11.54) * mm, "end": v(96, 10.54) * mm});
            skLineSegment(sketch, "E9.4.0.17", {"start": v(85.54, 0.02) * mm, "end": v(85.54, 0.04) * mm});
            skLineSegment(sketch, "E9.4.0.18", {"start": v(84.54, 0.02) * mm, "end": v(84.54, 0.04) * mm});
            skLineSegment(sketch, "E9.4.0.19", {"start": v(84.54, 0.04) * mm, "end": v(85.54, 0.04) * mm});
            skLineSegment(sketch, "E9.4.1.0", {"start": v(96.04, 46) * mm, "end": v(96.02, 35.54) * mm});
            skLineSegment(sketch, "E9.4.1.1", {"start": v(96.02, 34.54) * mm, "end": v(96, 24) * mm});
            skLineSegment(sketch, "E9.4.1.2", {"start": v(74.04, 46.04) * mm, "end": v(74.02, 35.54) * mm});
            skLineSegment(sketch, "E9.4.1.3", {"start": v(74, 24.04) * mm, "end": v(84.54, 24.02) * mm});
            skLineSegment(sketch, "E9.4.1.4", {"start": v(74.04, 46.04) * mm, "end": v(84.54, 46.02) * mm});
            skLineSegment(sketch, "E9.4.1.5", {"start": v(85.54, 46.02) * mm, "end": v(96.04, 46) * mm});
            skLineSegment(sketch, "E9.4.1.6", {"start": v(74.02, 34.54) * mm, "end": v(74, 24.04) * mm});
            skLineSegment(sketch, "E9.4.1.7", {"start": v(85.54, 24.02) * mm, "end": v(96, 24) * mm});
            skLineSegment(sketch, "E9.4.1.8", {"start": v(84.54, 46.02) * mm, "end": v(84.54, 46) * mm});
            skLineSegment(sketch, "E9.4.1.9", {"start": v(84.54, 46) * mm, "end": v(85.54, 46) * mm});
            skLineSegment(sketch, "E9.4.1.10", {"start": v(85.54, 46.02) * mm, "end": v(85.54, 46) * mm});
            skLineSegment(sketch, "E9.4.1.11", {"start": v(74.04, 35.54) * mm, "end": v(74.04, 34.54) * mm});
            skLineSegment(sketch, "E9.4.1.12", {"start": v(74.02, 35.54) * mm, "end": v(74.04, 35.54) * mm});
            skLineSegment(sketch, "E9.4.1.13", {"start": v(74.02, 34.54) * mm, "end": v(74.04, 34.54) * mm});
            skLineSegment(sketch, "E9.4.1.14", {"start": v(96.02, 34.54) * mm, "end": v(96, 34.54) * mm});
            skLineSegment(sketch, "E9.4.1.15", {"start": v(96.02, 35.54) * mm, "end": v(96, 35.54) * mm});
            skLineSegment(sketch, "E9.4.1.16", {"start": v(96, 35.54) * mm, "end": v(96, 34.54) * mm});
            skLineSegment(sketch, "E9.4.1.17", {"start": v(85.54, 24.02) * mm, "end": v(85.54, 24.04) * mm});
            skLineSegment(sketch, "E9.4.1.18", {"start": v(84.54, 24.02) * mm, "end": v(84.54, 24.04) * mm});
            skLineSegment(sketch, "E9.4.1.19", {"start": v(84.54, 24.04) * mm, "end": v(85.54, 24.04) * mm});
            skLineSegment(sketch, "E9.4.2.0", {"start": v(96.04, 70) * mm, "end": v(96.02, 59.54) * mm});
            skLineSegment(sketch, "E9.4.2.1", {"start": v(96.02, 58.54) * mm, "end": v(96, 48) * mm});
            skLineSegment(sketch, "E9.4.2.2", {"start": v(74.04, 70.04) * mm, "end": v(74.02, 59.54) * mm});
            skLineSegment(sketch, "E9.4.2.3", {"start": v(74, 48.04) * mm, "end": v(84.54, 48.02) * mm});
            skLineSegment(sketch, "E9.4.2.4", {"start": v(74.04, 70.04) * mm, "end": v(84.54, 70.02) * mm});
            skLineSegment(sketch, "E9.4.2.5", {"start": v(85.54, 70.02) * mm, "end": v(96.04, 70) * mm});
            skLineSegment(sketch, "E9.4.2.6", {"start": v(74.02, 58.54) * mm, "end": v(74, 48.04) * mm});
            skLineSegment(sketch, "E9.4.2.7", {"start": v(85.54, 48.02) * mm, "end": v(96, 48) * mm});
            skLineSegment(sketch, "E9.4.2.8", {"start": v(84.54, 70.02) * mm, "end": v(84.54, 70) * mm});
            skLineSegment(sketch, "E9.4.2.9", {"start": v(84.54, 70) * mm, "end": v(85.54, 70) * mm});
            skLineSegment(sketch, "E9.4.2.10", {"start": v(85.54, 70.02) * mm, "end": v(85.54, 70) * mm});
            skLineSegment(sketch, "E9.4.2.11", {"start": v(74.04, 59.54) * mm, "end": v(74.04, 58.54) * mm});
            skLineSegment(sketch, "E9.4.2.12", {"start": v(74.02, 59.54) * mm, "end": v(74.04, 59.54) * mm});
            skLineSegment(sketch, "E9.4.2.13", {"start": v(74.02, 58.54) * mm, "end": v(74.04, 58.54) * mm});
            skLineSegment(sketch, "E9.4.2.14", {"start": v(96.02, 58.54) * mm, "end": v(96, 58.54) * mm});
            skLineSegment(sketch, "E9.4.2.15", {"start": v(96.02, 59.54) * mm, "end": v(96, 59.54) * mm});
            skLineSegment(sketch, "E9.4.2.16", {"start": v(96, 59.54) * mm, "end": v(96, 58.54) * mm});
            skLineSegment(sketch, "E9.4.2.17", {"start": v(85.54, 48.02) * mm, "end": v(85.54, 48.04) * mm});
            skLineSegment(sketch, "E9.4.2.18", {"start": v(84.54, 48.02) * mm, "end": v(84.54, 48.04) * mm});
            skLineSegment(sketch, "E9.4.2.19", {"start": v(84.54, 48.04) * mm, "end": v(85.54, 48.04) * mm});
            skLineSegment(sketch, "E9.4.3.0", {"start": v(96.04, 94) * mm, "end": v(96.02, 83.54) * mm});
            skLineSegment(sketch, "E9.4.3.1", {"start": v(96.02, 82.54) * mm, "end": v(96, 72) * mm});
            skLineSegment(sketch, "E9.4.3.2", {"start": v(74.04, 94.04) * mm, "end": v(74.02, 83.54) * mm});
            skLineSegment(sketch, "E9.4.3.3", {"start": v(74, 72.04) * mm, "end": v(84.54, 72.02) * mm});
            skLineSegment(sketch, "E9.4.3.4", {"start": v(74.04, 94.04) * mm, "end": v(84.54, 94.02) * mm});
            skLineSegment(sketch, "E9.4.3.5", {"start": v(85.54, 94.02) * mm, "end": v(96.04, 94) * mm});
            skLineSegment(sketch, "E9.4.3.6", {"start": v(74.02, 82.54) * mm, "end": v(74, 72.04) * mm});
            skLineSegment(sketch, "E9.4.3.7", {"start": v(85.54, 72.02) * mm, "end": v(96, 72) * mm});
            skLineSegment(sketch, "E9.4.3.8", {"start": v(84.54, 94.02) * mm, "end": v(84.54, 94) * mm});
            skLineSegment(sketch, "E9.4.3.9", {"start": v(84.54, 94) * mm, "end": v(85.54, 94) * mm});
            skLineSegment(sketch, "E9.4.3.10", {"start": v(85.54, 94.02) * mm, "end": v(85.54, 94) * mm});
            skLineSegment(sketch, "E9.4.3.11", {"start": v(74.04, 83.54) * mm, "end": v(74.04, 82.54) * mm});
            skLineSegment(sketch, "E9.4.3.12", {"start": v(74.02, 83.54) * mm, "end": v(74.04, 83.54) * mm});
            skLineSegment(sketch, "E9.4.3.13", {"start": v(74.02, 82.54) * mm, "end": v(74.04, 82.54) * mm});
            skLineSegment(sketch, "E9.4.3.14", {"start": v(96.02, 82.54) * mm, "end": v(96, 82.54) * mm});
            skLineSegment(sketch, "E9.4.3.15", {"start": v(96.02, 83.54) * mm, "end": v(96, 83.54) * mm});
            skLineSegment(sketch, "E9.4.3.16", {"start": v(96, 83.54) * mm, "end": v(96, 82.54) * mm});
            skLineSegment(sketch, "E9.4.3.17", {"start": v(85.54, 72.02) * mm, "end": v(85.54, 72.04) * mm});
            skLineSegment(sketch, "E9.4.3.18", {"start": v(84.54, 72.02) * mm, "end": v(84.54, 72.04) * mm});
            skLineSegment(sketch, "E9.4.3.19", {"start": v(84.54, 72.04) * mm, "end": v(85.54, 72.04) * mm});
            skLineSegment(sketch, "E9.5.0.0", {"start": v(120.04, 22) * mm, "end": v(120.02, 11.54) * mm});
            skLineSegment(sketch, "E9.5.0.1", {"start": v(120.02, 10.54) * mm, "end": v(120, 0) * mm});
            skLineSegment(sketch, "E9.5.0.2", {"start": v(98.04, 22.04) * mm, "end": v(98.02, 11.54) * mm});
            skLineSegment(sketch, "E9.5.0.3", {"start": v(98, 0.04) * mm, "end": v(108.54, 0.02) * mm});
            skLineSegment(sketch, "E9.5.0.4", {"start": v(98.04, 22.04) * mm, "end": v(108.54, 22.02) * mm});
            skLineSegment(sketch, "E9.5.0.5", {"start": v(109.54, 22.02) * mm, "end": v(120.04, 22) * mm});
            skLineSegment(sketch, "E9.5.0.6", {"start": v(98.02, 10.54) * mm, "end": v(98, 0.04) * mm});
            skLineSegment(sketch, "E9.5.0.7", {"start": v(109.54, 0.02) * mm, "end": v(120, 0) * mm});
            skLineSegment(sketch, "E9.5.0.8", {"start": v(108.54, 22.02) * mm, "end": v(108.54, 22) * mm});
            skLineSegment(sketch, "E9.5.0.9", {"start": v(108.54, 22) * mm, "end": v(109.54, 22) * mm});
            skLineSegment(sketch, "E9.5.0.10", {"start": v(109.54, 22.02) * mm, "end": v(109.54, 22) * mm});
            skLineSegment(sketch, "E9.5.0.11", {"start": v(98.04, 11.54) * mm, "end": v(98.04, 10.54) * mm});
            skLineSegment(sketch, "E9.5.0.12", {"start": v(98.02, 11.54) * mm, "end": v(98.04, 11.54) * mm});
            skLineSegment(sketch, "E9.5.0.13", {"start": v(98.02, 10.54) * mm, "end": v(98.04, 10.54) * mm});
            skLineSegment(sketch, "E9.5.0.14", {"start": v(120.02, 10.54) * mm, "end": v(120, 10.54) * mm});
            skLineSegment(sketch, "E9.5.0.15", {"start": v(120.02, 11.54) * mm, "end": v(120, 11.54) * mm});
            skLineSegment(sketch, "E9.5.0.16", {"start": v(120, 11.54) * mm, "end": v(120, 10.54) * mm});
            skLineSegment(sketch, "E9.5.0.17", {"start": v(109.54, 0.02) * mm, "end": v(109.54, 0.04) * mm});
            skLineSegment(sketch, "E9.5.0.18", {"start": v(108.54, 0.02) * mm, "end": v(108.54, 0.04) * mm});
            skLineSegment(sketch, "E9.5.0.19", {"start": v(108.54, 0.04) * mm, "end": v(109.54, 0.04) * mm});
            skLineSegment(sketch, "E9.5.1.0", {"start": v(120.04, 46) * mm, "end": v(120.02, 35.54) * mm});
            skLineSegment(sketch, "E9.5.1.1", {"start": v(120.02, 34.54) * mm, "end": v(120, 24) * mm});
            skLineSegment(sketch, "E9.5.1.2", {"start": v(98.04, 46.04) * mm, "end": v(98.02, 35.54) * mm});
            skLineSegment(sketch, "E9.5.1.3", {"start": v(98, 24.04) * mm, "end": v(108.54, 24.02) * mm});
            skLineSegment(sketch, "E9.5.1.4", {"start": v(98.04, 46.04) * mm, "end": v(108.54, 46.02) * mm});
            skLineSegment(sketch, "E9.5.1.5", {"start": v(109.54, 46.02) * mm, "end": v(120.04, 46) * mm});
            skLineSegment(sketch, "E9.5.1.6", {"start": v(98.02, 34.54) * mm, "end": v(98, 24.04) * mm});
            skLineSegment(sketch, "E9.5.1.7", {"start": v(109.54, 24.02) * mm, "end": v(120, 24) * mm});
            skLineSegment(sketch, "E9.5.1.8", {"start": v(108.54, 46.02) * mm, "end": v(108.54, 46) * mm});
            skLineSegment(sketch, "E9.5.1.9", {"start": v(108.54, 46) * mm, "end": v(109.54, 46) * mm});
            skLineSegment(sketch, "E9.5.1.10", {"start": v(109.54, 46.02) * mm, "end": v(109.54, 46) * mm});
            skLineSegment(sketch, "E9.5.1.11", {"start": v(98.04, 35.54) * mm, "end": v(98.04, 34.54) * mm});
            skLineSegment(sketch, "E9.5.1.12", {"start": v(98.02, 35.54) * mm, "end": v(98.04, 35.54) * mm});
            skLineSegment(sketch, "E9.5.1.13", {"start": v(98.02, 34.54) * mm, "end": v(98.04, 34.54) * mm});
            skLineSegment(sketch, "E9.5.1.14", {"start": v(120.02, 34.54) * mm, "end": v(120, 34.54) * mm});
            skLineSegment(sketch, "E9.5.1.15", {"start": v(120.02, 35.54) * mm, "end": v(120, 35.54) * mm});
            skLineSegment(sketch, "E9.5.1.16", {"start": v(120, 35.54) * mm, "end": v(120, 34.54) * mm});
            skLineSegment(sketch, "E9.5.1.17", {"start": v(109.54, 24.02) * mm, "end": v(109.54, 24.04) * mm});
            skLineSegment(sketch, "E9.5.1.18", {"start": v(108.54, 24.02) * mm, "end": v(108.54, 24.04) * mm});
            skLineSegment(sketch, "E9.5.1.19", {"start": v(108.54, 24.04) * mm, "end": v(109.54, 24.04) * mm});
            skLineSegment(sketch, "E9.5.2.0", {"start": v(120.04, 70) * mm, "end": v(120.02, 59.54) * mm});
            skLineSegment(sketch, "E9.5.2.1", {"start": v(120.02, 58.54) * mm, "end": v(120, 48) * mm});
            skLineSegment(sketch, "E9.5.2.2", {"start": v(98.04, 70.04) * mm, "end": v(98.02, 59.54) * mm});
            skLineSegment(sketch, "E9.5.2.3", {"start": v(98, 48.04) * mm, "end": v(108.54, 48.02) * mm});
            skLineSegment(sketch, "E9.5.2.4", {"start": v(98.04, 70.04) * mm, "end": v(108.54, 70.02) * mm});
            skLineSegment(sketch, "E9.5.2.5", {"start": v(109.54, 70.02) * mm, "end": v(120.04, 70) * mm});
            skLineSegment(sketch, "E9.5.2.6", {"start": v(98.02, 58.54) * mm, "end": v(98, 48.04) * mm});
            skLineSegment(sketch, "E9.5.2.7", {"start": v(109.54, 48.02) * mm, "end": v(120, 48) * mm});
            skLineSegment(sketch, "E9.5.2.8", {"start": v(108.54, 70.02) * mm, "end": v(108.54, 70) * mm});
            skLineSegment(sketch, "E9.5.2.9", {"start": v(108.54, 70) * mm, "end": v(109.54, 70) * mm});
            skLineSegment(sketch, "E9.5.2.10", {"start": v(109.54, 70.02) * mm, "end": v(109.54, 70) * mm});
            skLineSegment(sketch, "E9.5.2.11", {"start": v(98.04, 59.54) * mm, "end": v(98.04, 58.54) * mm});
            skLineSegment(sketch, "E9.5.2.12", {"start": v(98.02, 59.54) * mm, "end": v(98.04, 59.54) * mm});
            skLineSegment(sketch, "E9.5.2.13", {"start": v(98.02, 58.54) * mm, "end": v(98.04, 58.54) * mm});
            skLineSegment(sketch, "E9.5.2.14", {"start": v(120.02, 58.54) * mm, "end": v(120, 58.54) * mm});
            skLineSegment(sketch, "E9.5.2.15", {"start": v(120.02, 59.54) * mm, "end": v(120, 59.54) * mm});
            skLineSegment(sketch, "E9.5.2.16", {"start": v(120, 59.54) * mm, "end": v(120, 58.54) * mm});
            skLineSegment(sketch, "E9.5.2.17", {"start": v(109.54, 48.02) * mm, "end": v(109.54, 48.04) * mm});
            skLineSegment(sketch, "E9.5.2.18", {"start": v(108.54, 48.02) * mm, "end": v(108.54, 48.04) * mm});
            skLineSegment(sketch, "E9.5.2.19", {"start": v(108.54, 48.04) * mm, "end": v(109.54, 48.04) * mm});
            skLineSegment(sketch, "E9.5.3.0", {"start": v(120.04, 94) * mm, "end": v(120.02, 83.54) * mm});
            skLineSegment(sketch, "E9.5.3.1", {"start": v(120.02, 82.54) * mm, "end": v(120, 72) * mm});
            skLineSegment(sketch, "E9.5.3.2", {"start": v(98.04, 94.04) * mm, "end": v(98.02, 83.54) * mm});
            skLineSegment(sketch, "E9.5.3.3", {"start": v(98, 72.04) * mm, "end": v(108.54, 72.02) * mm});
            skLineSegment(sketch, "E9.5.3.4", {"start": v(98.04, 94.04) * mm, "end": v(108.54, 94.02) * mm});
            skLineSegment(sketch, "E9.5.3.5", {"start": v(109.54, 94.02) * mm, "end": v(120.04, 94) * mm});
            skLineSegment(sketch, "E9.5.3.6", {"start": v(98.02, 82.54) * mm, "end": v(98, 72.04) * mm});
            skLineSegment(sketch, "E9.5.3.7", {"start": v(109.54, 72.02) * mm, "end": v(120, 72) * mm});
            skLineSegment(sketch, "E9.5.3.8", {"start": v(108.54, 94.02) * mm, "end": v(108.54, 94) * mm});
            skLineSegment(sketch, "E9.5.3.9", {"start": v(108.54, 94) * mm, "end": v(109.54, 94) * mm});
            skLineSegment(sketch, "E9.5.3.10", {"start": v(109.54, 94.02) * mm, "end": v(109.54, 94) * mm});
            skLineSegment(sketch, "E9.5.3.11", {"start": v(98.04, 83.54) * mm, "end": v(98.04, 82.54) * mm});
            skLineSegment(sketch, "E9.5.3.12", {"start": v(98.02, 83.54) * mm, "end": v(98.04, 83.54) * mm});
            skLineSegment(sketch, "E9.5.3.13", {"start": v(98.02, 82.54) * mm, "end": v(98.04, 82.54) * mm});
            skLineSegment(sketch, "E9.5.3.14", {"start": v(120.02, 82.54) * mm, "end": v(120, 82.54) * mm});
            skLineSegment(sketch, "E9.5.3.15", {"start": v(120.02, 83.54) * mm, "end": v(120, 83.54) * mm});
            skLineSegment(sketch, "E9.5.3.16", {"start": v(120, 83.54) * mm, "end": v(120, 82.54) * mm});
            skLineSegment(sketch, "E9.5.3.17", {"start": v(109.54, 72.02) * mm, "end": v(109.54, 72.04) * mm});
            skLineSegment(sketch, "E9.5.3.18", {"start": v(108.54, 72.02) * mm, "end": v(108.54, 72.04) * mm});
            skLineSegment(sketch, "E9.5.3.19", {"start": v(108.54, 72.04) * mm, "end": v(109.54, 72.04) * mm});
            skLineSegment(sketch, "E9.direction1", {"start": v(-22, 0.04) * mm, "end": v(2, 0.04) * mm, "construction": true});
            skLineSegment(sketch, "E9.direction2", {"start": v(-22, 0.04) * mm, "end": v(-22, 24.04) * mm, "construction": true});
            skLineSegment(sketch, "E10.bottom", {"start": v(-22.96, 95.04) * mm, "end": v(121, 95.04) * mm});
            skLineSegment(sketch, "E10.top", {"start": v(-22.96, -0.96) * mm, "end": v(121, -0.96) * mm});
            skLineSegment(sketch, "E10.left", {"start": v(-22.96, 95.04) * mm, "end": v(-22.96, -0.96) * mm});
            skLineSegment(sketch, "E10.right", {"start": v(121, 95.04) * mm, "end": v(121, -0.96) * mm});
            skSolve(sketch);
        }
        {
            var Q0;
            Q0 = qSketchRegion(id + "F0", true);
            extrude(context, id + "F1", {"entities" : qUnion([Q0]), "depth" : 45 * mm});
        }
        {
            var Q0;
            Q0=qCreatedBy(makeId("Top.planeOp"),FACE);
            var sketch = newSketch(context, id + "F2", { "sketchPlane" : qUnion([Q0])});
            skLineSegment(sketch, "E11.0", {"start": v(-23.96, 96.04) * mm, "end": v(122, 96.04) * mm});
            skLineSegment(sketch, "E11.1", {"start": v(-23.96, 96.04) * mm, "end": v(-23.96, -1.96) * mm});
            skLineSegment(sketch, "E11.2", {"start": v(-23.96, -1.96) * mm, "end": v(122, -1.96) * mm});
            skLineSegment(sketch, "E11.3", {"start": v(122, 96.04) * mm, "end": v(122, -1.96) * mm});
            skSolve(sketch);
        }
        {
            var Q0;
            Q0 = qSketchRegion(id + "F2", true);
            extrude(context, id + "F3", {"entities" : qUnion([Q0]), "operationType" : NewBodyOperationType.ADD, "oppositeDirection" : true, "depth" : 1 * mm});
        }
        {
            var Q0;
            {var subQ0=sQuery(id+"F2.wireOp",EDGE,"E11.0");var subQ1=sQuery(id+"F2.wireOp",EDGE,"E11.1");var subQ2=sQuery(id+"F2.wireOp",EDGE,"E11.2");var subQ3=sQuery(id+"F2.wireOp",EDGE,"E11.3");Q0=makeQuery(id+"F3.boolean.opBoolean","SPLIT",FACE,{"disambiguationData":[TD([makeQuery(id+"F1.opExtrude","SWEPT_FACE",FACE,{"disambiguationData":[OSD([sQuery(id+"F0.wireOp",EDGE,"E10.bottom")])]})])],"derivedFrom":makeQuery(id+"F3.opExtrude","CAP_FACE",FACE,{"disambiguationData":[OSD([subQ0,subQ1,subQ2,subQ3])],"isStart":true})});}
            var sketch = newSketch(context, id + "F4", { "sketchPlane" : qUnion([Q0])});
            skLineSegment(sketch, "E12.0", {"start": v(-23.96, 96.04) * mm, "end": v(-23.96, -1.96) * mm});
            skLineSegment(sketch, "E13.0", {"start": v(-22.96, 95.04) * mm, "end": v(-22.96, -0.96) * mm});
            skLineSegment(sketch, "E14.0", {"start": v(-23.96, 96.04) * mm, "end": v(122, 96.04) * mm});
            skLineSegment(sketch, "E15.0", {"start": v(-22.96, 95.04) * mm, "end": v(121, 95.04) * mm});
            skLineSegment(sketch, "E16.0", {"start": v(122, 96.04) * mm, "end": v(122, -1.96) * mm});
            skLineSegment(sketch, "E17.0", {"start": v(121, 95.04) * mm, "end": v(121, -0.96) * mm});
            skLineSegment(sketch, "E18.0", {"start": v(-23.96, -1.96) * mm, "end": v(122, -1.96) * mm});
            skLineSegment(sketch, "E19.0", {"start": v(-22.96, -0.96) * mm, "end": v(121, -0.96) * mm});
            skSolve(sketch);
        }
        {
            var Q0;
            Q0 = qSketchRegion(id + "F4", true);
            var Q1;
            Q1=makeQuery(id+"F1.opExtrude","CAP_FACE",FACE,{"disambiguationData":[OSD([sQuery(id+"F0.wireOp",EDGE,"E0.bottom"),sQuery(id+"F0.wireOp",EDGE,"E0.top"),sQuery(id+"F0.wireOp",EDGE,"E0.left"),sQuery(id+"F0.wireOp",EDGE,"E0.right"),sQuery(id+"F0.wireOp",EDGE,"E1.top"),sQuery(id+"F0.wireOp",EDGE,"E1.left"),sQuery(id+"F0.wireOp",EDGE,"E1.right"),sQuery(id+"F0.wireOp",EDGE,"E2.bottom"),sQuery(id+"F0.wireOp",EDGE,"E2.top"),sQuery(id+"F0.wireOp",EDGE,"E2.right"),sQuery(id+"F0.wireOp",EDGE,"E3.bottom"),sQuery(id+"F0.wireOp",EDGE,"E3.top"),sQuery(id+"F0.wireOp",EDGE,"E3.right"),sQuery(id+"F0.wireOp",EDGE,"E4.top"),sQuery(id+"F0.wireOp",EDGE,"E4.left"),sQuery(id+"F0.wireOp",EDGE,"E4.right"),sQuery(id+"F0.wireOp",EDGE,"E5.trimOffspring"),sQuery(id+"F0.wireOp",EDGE,"E6.trimOffspring"),sQuery(id+"F0.wireOp",EDGE,"E7.trimOffspring"),sQuery(id+"F0.wireOp",EDGE,"E8.trimOffspring"),sQuery(id+"F0.wireOp",EDGE,"E9.0.1.0"),sQuery(id+"F0.wireOp",EDGE,"E9.0.1.1"),sQuery(id+"F0.wireOp",EDGE,"E9.0.1.2"),sQuery(id+"F0.wireOp",EDGE,"E9.0.1.3"),sQuery(id+"F0.wireOp",EDGE,"E9.0.1.4"),sQuery(id+"F0.wireOp",EDGE,"E9.0.1.5"),sQuery(id+"F0.wireOp",EDGE,"E9.0.1.6"),sQuery(id+"F0.wireOp",EDGE,"E9.0.1.7"),sQuery(id+"F0.wireOp",EDGE,"E9.0.1.8"),sQuery(id+"F0.wireOp",EDGE,"E9.0.1.9"),sQuery(id+"F0.wireOp",EDGE,"E9.0.1.10"),sQuery(id+"F0.wireOp",EDGE,"E9.0.1.11"),sQuery(id+"F0.wireOp",EDGE,"E9.0.1.12"),sQuery(id+"F0.wireOp",EDGE,"E9.0.1.13"),sQuery(id+"F0.wireOp",EDGE,"E9.0.1.14"),sQuery(id+"F0.wireOp",EDGE,"E9.0.1.15"),sQuery(id+"F0.wireOp",EDGE,"E9.0.1.16"),sQuery(id+"F0.wireOp",EDGE,"E9.0.1.17"),sQuery(id+"F0.wireOp",EDGE,"E9.0.1.18"),sQuery(id+"F0.wireOp",EDGE,"E9.0.1.19"),sQuery(id+"F0.wireOp",EDGE,"E9.0.2.0"),sQuery(id+"F0.wireOp",EDGE,"E9.0.2.1"),sQuery(id+"F0.wireOp",EDGE,"E9.0.2.2"),sQuery(id+"F0.wireOp",EDGE,"E9.0.2.3"),sQuery(id+"F0.wireOp",EDGE,"E9.0.2.4"),sQuery(id+"F0.wireOp",EDGE,"E9.0.2.5"),sQuery(id+"F0.wireOp",EDGE,"E9.0.2.6"),sQuery(id+"F0.wireOp",EDGE,"E9.0.2.7"),sQuery(id+"F0.wireOp",EDGE,"E9.0.2.8"),sQuery(id+"F0.wireOp",EDGE,"E9.0.2.9"),sQuery(id+"F0.wireOp",EDGE,"E9.0.2.10"),sQuery(id+"F0.wireOp",EDGE,"E9.0.2.11"),sQuery(id+"F0.wireOp",EDGE,"E9.0.2.12"),sQuery(id+"F0.wireOp",EDGE,"E9.0.2.13"),sQuery(id+"F0.wireOp",EDGE,"E9.0.2.14"),sQuery(id+"F0.wireOp",EDGE,"E9.0.2.15"),sQuery(id+"F0.wireOp",EDGE,"E9.0.2.16"),sQuery(id+"F0.wireOp",EDGE,"E9.0.2.17"),sQuery(id+"F0.wireOp",EDGE,"E9.0.2.18"),sQuery(id+"F0.wireOp",EDGE,"E9.0.2.19"),sQuery(id+"F0.wireOp",EDGE,"E9.0.3.0"),sQuery(id+"F0.wireOp",EDGE,"E9.0.3.1"),sQuery(id+"F0.wireOp",EDGE,"E9.0.3.2"),sQuery(id+"F0.wireOp",EDGE,"E9.0.3.3"),sQuery(id+"F0.wireOp",EDGE,"E9.0.3.4"),sQuery(id+"F0.wireOp",EDGE,"E9.0.3.5"),sQuery(id+"F0.wireOp",EDGE,"E9.0.3.6"),sQuery(id+"F0.wireOp",EDGE,"E9.0.3.7"),sQuery(id+"F0.wireOp",EDGE,"E9.0.3.8"),sQuery(id+"F0.wireOp",EDGE,"E9.0.3.9"),sQuery(id+"F0.wireOp",EDGE,"E9.0.3.10"),sQuery(id+"F0.wireOp",EDGE,"E9.0.3.11"),sQuery(id+"F0.wireOp",EDGE,"E9.0.3.12"),sQuery(id+"F0.wireOp",EDGE,"E9.0.3.13"),sQuery(id+"F0.wireOp",EDGE,"E9.0.3.14"),sQuery(id+"F0.wireOp",EDGE,"E9.0.3.15"),sQuery(id+"F0.wireOp",EDGE,"E9.0.3.16"),sQuery(id+"F0.wireOp",EDGE,"E9.0.3.17"),sQuery(id+"F0.wireOp",EDGE,"E9.0.3.18"),sQuery(id+"F0.wireOp",EDGE,"E9.0.3.19"),sQuery(id+"F0.wireOp",EDGE,"E9.1.0.0"),sQuery(id+"F0.wireOp",EDGE,"E9.1.0.1"),sQuery(id+"F0.wireOp",EDGE,"E9.1.0.2"),sQuery(id+"F0.wireOp",EDGE,"E9.1.0.3"),sQuery(id+"F0.wireOp",EDGE,"E9.1.0.4"),sQuery(id+"F0.wireOp",EDGE,"E9.1.0.5"),sQuery(id+"F0.wireOp",EDGE,"E9.1.0.6"),sQuery(id+"F0.wireOp",EDGE,"E9.1.0.7"),sQuery(id+"F0.wireOp",EDGE,"E9.1.0.8"),sQuery(id+"F0.wireOp",EDGE,"E9.1.0.9"),sQuery(id+"F0.wireOp",EDGE,"E9.1.0.10"),sQuery(id+"F0.wireOp",EDGE,"E9.1.0.11"),sQuery(id+"F0.wireOp",EDGE,"E9.1.0.12"),sQuery(id+"F0.wireOp",EDGE,"E9.1.0.13"),sQuery(id+"F0.wireOp",EDGE,"E9.1.0.14"),sQuery(id+"F0.wireOp",EDGE,"E9.1.0.15"),sQuery(id+"F0.wireOp",EDGE,"E9.1.0.16"),sQuery(id+"F0.wireOp",EDGE,"E9.1.0.17"),sQuery(id+"F0.wireOp",EDGE,"E9.1.0.18"),sQuery(id+"F0.wireOp",EDGE,"E9.1.0.19"),sQuery(id+"F0.wireOp",EDGE,"E9.1.1.0"),sQuery(id+"F0.wireOp",EDGE,"E9.1.1.1"),sQuery(id+"F0.wireOp",EDGE,"E9.1.1.2"),sQuery(id+"F0.wireOp",EDGE,"E9.1.1.3"),sQuery(id+"F0.wireOp",EDGE,"E9.1.1.4"),sQuery(id+"F0.wireOp",EDGE,"E9.1.1.5"),sQuery(id+"F0.wireOp",EDGE,"E9.1.1.6"),sQuery(id+"F0.wireOp",EDGE,"E9.1.1.7"),sQuery(id+"F0.wireOp",EDGE,"E9.1.1.8"),sQuery(id+"F0.wireOp",EDGE,"E9.1.1.9"),sQuery(id+"F0.wireOp",EDGE,"E9.1.1.10"),sQuery(id+"F0.wireOp",EDGE,"E9.1.1.11"),sQuery(id+"F0.wireOp",EDGE,"E9.1.1.12"),sQuery(id+"F0.wireOp",EDGE,"E9.1.1.13"),sQuery(id+"F0.wireOp",EDGE,"E9.1.1.14"),sQuery(id+"F0.wireOp",EDGE,"E9.1.1.15"),sQuery(id+"F0.wireOp",EDGE,"E9.1.1.16"),sQuery(id+"F0.wireOp",EDGE,"E9.1.1.17"),sQuery(id+"F0.wireOp",EDGE,"E9.1.1.18"),sQuery(id+"F0.wireOp",EDGE,"E9.1.1.19"),sQuery(id+"F0.wireOp",EDGE,"E9.1.2.0"),sQuery(id+"F0.wireOp",EDGE,"E9.1.2.1"),sQuery(id+"F0.wireOp",EDGE,"E9.1.2.2"),sQuery(id+"F0.wireOp",EDGE,"E9.1.2.3"),sQuery(id+"F0.wireOp",EDGE,"E9.1.2.4"),sQuery(id+"F0.wireOp",EDGE,"E9.1.2.5"),sQuery(id+"F0.wireOp",EDGE,"E9.1.2.6"),sQuery(id+"F0.wireOp",EDGE,"E9.1.2.7"),sQuery(id+"F0.wireOp",EDGE,"E9.1.2.8"),sQuery(id+"F0.wireOp",EDGE,"E9.1.2.9"),sQuery(id+"F0.wireOp",EDGE,"E9.1.2.10"),sQuery(id+"F0.wireOp",EDGE,"E9.1.2.11"),sQuery(id+"F0.wireOp",EDGE,"E9.1.2.12"),sQuery(id+"F0.wireOp",EDGE,"E9.1.2.13"),sQuery(id+"F0.wireOp",EDGE,"E9.1.2.14"),sQuery(id+"F0.wireOp",EDGE,"E9.1.2.15"),sQuery(id+"F0.wireOp",EDGE,"E9.1.2.16"),sQuery(id+"F0.wireOp",EDGE,"E9.1.2.17"),sQuery(id+"F0.wireOp",EDGE,"E9.1.2.18"),sQuery(id+"F0.wireOp",EDGE,"E9.1.2.19"),sQuery(id+"F0.wireOp",EDGE,"E9.1.3.0"),sQuery(id+"F0.wireOp",EDGE,"E9.1.3.1"),sQuery(id+"F0.wireOp",EDGE,"E9.1.3.2"),sQuery(id+"F0.wireOp",EDGE,"E9.1.3.3"),sQuery(id+"F0.wireOp",EDGE,"E9.1.3.4"),sQuery(id+"F0.wireOp",EDGE,"E9.1.3.5"),sQuery(id+"F0.wireOp",EDGE,"E9.1.3.6"),sQuery(id+"F0.wireOp",EDGE,"E9.1.3.7"),sQuery(id+"F0.wireOp",EDGE,"E9.1.3.8"),sQuery(id+"F0.wireOp",EDGE,"E9.1.3.9"),sQuery(id+"F0.wireOp",EDGE,"E9.1.3.10"),sQuery(id+"F0.wireOp",EDGE,"E9.1.3.11"),sQuery(id+"F0.wireOp",EDGE,"E9.1.3.12"),sQuery(id+"F0.wireOp",EDGE,"E9.1.3.13"),sQuery(id+"F0.wireOp",EDGE,"E9.1.3.14"),sQuery(id+"F0.wireOp",EDGE,"E9.1.3.15"),sQuery(id+"F0.wireOp",EDGE,"E9.1.3.16"),sQuery(id+"F0.wireOp",EDGE,"E9.1.3.17"),sQuery(id+"F0.wireOp",EDGE,"E9.1.3.18"),sQuery(id+"F0.wireOp",EDGE,"E9.1.3.19"),sQuery(id+"F0.wireOp",EDGE,"E9.2.0.0"),sQuery(id+"F0.wireOp",EDGE,"E9.2.0.1"),sQuery(id+"F0.wireOp",EDGE,"E9.2.0.2"),sQuery(id+"F0.wireOp",EDGE,"E9.2.0.3"),sQuery(id+"F0.wireOp",EDGE,"E9.2.0.4"),sQuery(id+"F0.wireOp",EDGE,"E9.2.0.5"),sQuery(id+"F0.wireOp",EDGE,"E9.2.0.6"),sQuery(id+"F0.wireOp",EDGE,"E9.2.0.7"),sQuery(id+"F0.wireOp",EDGE,"E9.2.0.8"),sQuery(id+"F0.wireOp",EDGE,"E9.2.0.9"),sQuery(id+"F0.wireOp",EDGE,"E9.2.0.10"),sQuery(id+"F0.wireOp",EDGE,"E9.2.0.11"),sQuery(id+"F0.wireOp",EDGE,"E9.2.0.12"),sQuery(id+"F0.wireOp",EDGE,"E9.2.0.13"),sQuery(id+"F0.wireOp",EDGE,"E9.2.0.14"),sQuery(id+"F0.wireOp",EDGE,"E9.2.0.15"),sQuery(id+"F0.wireOp",EDGE,"E9.2.0.16"),sQuery(id+"F0.wireOp",EDGE,"E9.2.0.17"),sQuery(id+"F0.wireOp",EDGE,"E9.2.0.18"),sQuery(id+"F0.wireOp",EDGE,"E9.2.0.19"),sQuery(id+"F0.wireOp",EDGE,"E9.2.1.0"),sQuery(id+"F0.wireOp",EDGE,"E9.2.1.1"),sQuery(id+"F0.wireOp",EDGE,"E9.2.1.2"),sQuery(id+"F0.wireOp",EDGE,"E9.2.1.3"),sQuery(id+"F0.wireOp",EDGE,"E9.2.1.4"),sQuery(id+"F0.wireOp",EDGE,"E9.2.1.5"),sQuery(id+"F0.wireOp",EDGE,"E9.2.1.6"),sQuery(id+"F0.wireOp",EDGE,"E9.2.1.7"),sQuery(id+"F0.wireOp",EDGE,"E9.2.1.8"),sQuery(id+"F0.wireOp",EDGE,"E9.2.1.9"),sQuery(id+"F0.wireOp",EDGE,"E9.2.1.10"),sQuery(id+"F0.wireOp",EDGE,"E9.2.1.11"),sQuery(id+"F0.wireOp",EDGE,"E9.2.1.12"),sQuery(id+"F0.wireOp",EDGE,"E9.2.1.13"),sQuery(id+"F0.wireOp",EDGE,"E9.2.1.14"),sQuery(id+"F0.wireOp",EDGE,"E9.2.1.15"),sQuery(id+"F0.wireOp",EDGE,"E9.2.1.16"),sQuery(id+"F0.wireOp",EDGE,"E9.2.1.17"),sQuery(id+"F0.wireOp",EDGE,"E9.2.1.18"),sQuery(id+"F0.wireOp",EDGE,"E9.2.1.19"),sQuery(id+"F0.wireOp",EDGE,"E9.2.2.0"),sQuery(id+"F0.wireOp",EDGE,"E9.2.2.1"),sQuery(id+"F0.wireOp",EDGE,"E9.2.2.2"),sQuery(id+"F0.wireOp",EDGE,"E9.2.2.3"),sQuery(id+"F0.wireOp",EDGE,"E9.2.2.4"),sQuery(id+"F0.wireOp",EDGE,"E9.2.2.5"),sQuery(id+"F0.wireOp",EDGE,"E9.2.2.6"),sQuery(id+"F0.wireOp",EDGE,"E9.2.2.7"),sQuery(id+"F0.wireOp",EDGE,"E9.2.2.8"),sQuery(id+"F0.wireOp",EDGE,"E9.2.2.9"),sQuery(id+"F0.wireOp",EDGE,"E9.2.2.10"),sQuery(id+"F0.wireOp",EDGE,"E9.2.2.11"),sQuery(id+"F0.wireOp",EDGE,"E9.2.2.12"),sQuery(id+"F0.wireOp",EDGE,"E9.2.2.13"),sQuery(id+"F0.wireOp",EDGE,"E9.2.2.14"),sQuery(id+"F0.wireOp",EDGE,"E9.2.2.15"),sQuery(id+"F0.wireOp",EDGE,"E9.2.2.16"),sQuery(id+"F0.wireOp",EDGE,"E9.2.2.17"),sQuery(id+"F0.wireOp",EDGE,"E9.2.2.18"),sQuery(id+"F0.wireOp",EDGE,"E9.2.2.19"),sQuery(id+"F0.wireOp",EDGE,"E9.2.3.0"),sQuery(id+"F0.wireOp",EDGE,"E9.2.3.1"),sQuery(id+"F0.wireOp",EDGE,"E9.2.3.2"),sQuery(id+"F0.wireOp",EDGE,"E9.2.3.3"),sQuery(id+"F0.wireOp",EDGE,"E9.2.3.4"),sQuery(id+"F0.wireOp",EDGE,"E9.2.3.5"),sQuery(id+"F0.wireOp",EDGE,"E9.2.3.6"),sQuery(id+"F0.wireOp",EDGE,"E9.2.3.7"),sQuery(id+"F0.wireOp",EDGE,"E9.2.3.8"),sQuery(id+"F0.wireOp",EDGE,"E9.2.3.9"),sQuery(id+"F0.wireOp",EDGE,"E9.2.3.10"),sQuery(id+"F0.wireOp",EDGE,"E9.2.3.11"),sQuery(id+"F0.wireOp",EDGE,"E9.2.3.12"),sQuery(id+"F0.wireOp",EDGE,"E9.2.3.13"),sQuery(id+"F0.wireOp",EDGE,"E9.2.3.14"),sQuery(id+"F0.wireOp",EDGE,"E9.2.3.15"),sQuery(id+"F0.wireOp",EDGE,"E9.2.3.16"),sQuery(id+"F0.wireOp",EDGE,"E9.2.3.17"),sQuery(id+"F0.wireOp",EDGE,"E9.2.3.18"),sQuery(id+"F0.wireOp",EDGE,"E9.2.3.19"),sQuery(id+"F0.wireOp",EDGE,"E9.3.0.0"),sQuery(id+"F0.wireOp",EDGE,"E9.3.0.1"),sQuery(id+"F0.wireOp",EDGE,"E9.3.0.2"),sQuery(id+"F0.wireOp",EDGE,"E9.3.0.3"),sQuery(id+"F0.wireOp",EDGE,"E9.3.0.4"),sQuery(id+"F0.wireOp",EDGE,"E9.3.0.5"),sQuery(id+"F0.wireOp",EDGE,"E9.3.0.6"),sQuery(id+"F0.wireOp",EDGE,"E9.3.0.7"),sQuery(id+"F0.wireOp",EDGE,"E9.3.0.8"),sQuery(id+"F0.wireOp",EDGE,"E9.3.0.9"),sQuery(id+"F0.wireOp",EDGE,"E9.3.0.10"),sQuery(id+"F0.wireOp",EDGE,"E9.3.0.11"),sQuery(id+"F0.wireOp",EDGE,"E9.3.0.12"),sQuery(id+"F0.wireOp",EDGE,"E9.3.0.13"),sQuery(id+"F0.wireOp",EDGE,"E9.3.0.14"),sQuery(id+"F0.wireOp",EDGE,"E9.3.0.15"),sQuery(id+"F0.wireOp",EDGE,"E9.3.0.16"),sQuery(id+"F0.wireOp",EDGE,"E9.3.0.17"),sQuery(id+"F0.wireOp",EDGE,"E9.3.0.18"),sQuery(id+"F0.wireOp",EDGE,"E9.3.0.19"),sQuery(id+"F0.wireOp",EDGE,"E9.3.1.0"),sQuery(id+"F0.wireOp",EDGE,"E9.3.1.1"),sQuery(id+"F0.wireOp",EDGE,"E9.3.1.2"),sQuery(id+"F0.wireOp",EDGE,"E9.3.1.3"),sQuery(id+"F0.wireOp",EDGE,"E9.3.1.4"),sQuery(id+"F0.wireOp",EDGE,"E9.3.1.5"),sQuery(id+"F0.wireOp",EDGE,"E9.3.1.6"),sQuery(id+"F0.wireOp",EDGE,"E9.3.1.7"),sQuery(id+"F0.wireOp",EDGE,"E9.3.1.8"),sQuery(id+"F0.wireOp",EDGE,"E9.3.1.9"),sQuery(id+"F0.wireOp",EDGE,"E9.3.1.10"),sQuery(id+"F0.wireOp",EDGE,"E9.3.1.11"),sQuery(id+"F0.wireOp",EDGE,"E9.3.1.12"),sQuery(id+"F0.wireOp",EDGE,"E9.3.1.13"),sQuery(id+"F0.wireOp",EDGE,"E9.3.1.14"),sQuery(id+"F0.wireOp",EDGE,"E9.3.1.15"),sQuery(id+"F0.wireOp",EDGE,"E9.3.1.16"),sQuery(id+"F0.wireOp",EDGE,"E9.3.1.17"),sQuery(id+"F0.wireOp",EDGE,"E9.3.1.18"),sQuery(id+"F0.wireOp",EDGE,"E9.3.1.19"),sQuery(id+"F0.wireOp",EDGE,"E9.3.2.0"),sQuery(id+"F0.wireOp",EDGE,"E9.3.2.1"),sQuery(id+"F0.wireOp",EDGE,"E9.3.2.2"),sQuery(id+"F0.wireOp",EDGE,"E9.3.2.3"),sQuery(id+"F0.wireOp",EDGE,"E9.3.2.4"),sQuery(id+"F0.wireOp",EDGE,"E9.3.2.5"),sQuery(id+"F0.wireOp",EDGE,"E9.3.2.6"),sQuery(id+"F0.wireOp",EDGE,"E9.3.2.7"),sQuery(id+"F0.wireOp",EDGE,"E9.3.2.8"),sQuery(id+"F0.wireOp",EDGE,"E9.3.2.9"),sQuery(id+"F0.wireOp",EDGE,"E9.3.2.10"),sQuery(id+"F0.wireOp",EDGE,"E9.3.2.11"),sQuery(id+"F0.wireOp",EDGE,"E9.3.2.12"),sQuery(id+"F0.wireOp",EDGE,"E9.3.2.13"),sQuery(id+"F0.wireOp",EDGE,"E9.3.2.14"),sQuery(id+"F0.wireOp",EDGE,"E9.3.2.15"),sQuery(id+"F0.wireOp",EDGE,"E9.3.2.16"),sQuery(id+"F0.wireOp",EDGE,"E9.3.2.17"),sQuery(id+"F0.wireOp",EDGE,"E9.3.2.18"),sQuery(id+"F0.wireOp",EDGE,"E9.3.2.19"),sQuery(id+"F0.wireOp",EDGE,"E9.3.3.0"),sQuery(id+"F0.wireOp",EDGE,"E9.3.3.1"),sQuery(id+"F0.wireOp",EDGE,"E9.3.3.2"),sQuery(id+"F0.wireOp",EDGE,"E9.3.3.3"),sQuery(id+"F0.wireOp",EDGE,"E9.3.3.4"),sQuery(id+"F0.wireOp",EDGE,"E9.3.3.5"),sQuery(id+"F0.wireOp",EDGE,"E9.3.3.6"),sQuery(id+"F0.wireOp",EDGE,"E9.3.3.7"),sQuery(id+"F0.wireOp",EDGE,"E9.3.3.8"),sQuery(id+"F0.wireOp",EDGE,"E9.3.3.9"),sQuery(id+"F0.wireOp",EDGE,"E9.3.3.10"),sQuery(id+"F0.wireOp",EDGE,"E9.3.3.11"),sQuery(id+"F0.wireOp",EDGE,"E9.3.3.12"),sQuery(id+"F0.wireOp",EDGE,"E9.3.3.13"),sQuery(id+"F0.wireOp",EDGE,"E9.3.3.14"),sQuery(id+"F0.wireOp",EDGE,"E9.3.3.15"),sQuery(id+"F0.wireOp",EDGE,"E9.3.3.16"),sQuery(id+"F0.wireOp",EDGE,"E9.3.3.17"),sQuery(id+"F0.wireOp",EDGE,"E9.3.3.18"),sQuery(id+"F0.wireOp",EDGE,"E9.3.3.19"),sQuery(id+"F0.wireOp",EDGE,"E9.4.0.0"),sQuery(id+"F0.wireOp",EDGE,"E9.4.0.1"),sQuery(id+"F0.wireOp",EDGE,"E9.4.0.2"),sQuery(id+"F0.wireOp",EDGE,"E9.4.0.3"),sQuery(id+"F0.wireOp",EDGE,"E9.4.0.4"),sQuery(id+"F0.wireOp",EDGE,"E9.4.0.5"),sQuery(id+"F0.wireOp",EDGE,"E9.4.0.6"),sQuery(id+"F0.wireOp",EDGE,"E9.4.0.7"),sQuery(id+"F0.wireOp",EDGE,"E9.4.0.8"),sQuery(id+"F0.wireOp",EDGE,"E9.4.0.9"),sQuery(id+"F0.wireOp",EDGE,"E9.4.0.10"),sQuery(id+"F0.wireOp",EDGE,"E9.4.0.11"),sQuery(id+"F0.wireOp",EDGE,"E9.4.0.12"),sQuery(id+"F0.wireOp",EDGE,"E9.4.0.13"),sQuery(id+"F0.wireOp",EDGE,"E9.4.0.14"),sQuery(id+"F0.wireOp",EDGE,"E9.4.0.15"),sQuery(id+"F0.wireOp",EDGE,"E9.4.0.16"),sQuery(id+"F0.wireOp",EDGE,"E9.4.0.17"),sQuery(id+"F0.wireOp",EDGE,"E9.4.0.18"),sQuery(id+"F0.wireOp",EDGE,"E9.4.0.19"),sQuery(id+"F0.wireOp",EDGE,"E9.4.1.0"),sQuery(id+"F0.wireOp",EDGE,"E9.4.1.1"),sQuery(id+"F0.wireOp",EDGE,"E9.4.1.2"),sQuery(id+"F0.wireOp",EDGE,"E9.4.1.3"),sQuery(id+"F0.wireOp",EDGE,"E9.4.1.4"),sQuery(id+"F0.wireOp",EDGE,"E9.4.1.5"),sQuery(id+"F0.wireOp",EDGE,"E9.4.1.6"),sQuery(id+"F0.wireOp",EDGE,"E9.4.1.7"),sQuery(id+"F0.wireOp",EDGE,"E9.4.1.8"),sQuery(id+"F0.wireOp",EDGE,"E9.4.1.9"),sQuery(id+"F0.wireOp",EDGE,"E9.4.1.10"),sQuery(id+"F0.wireOp",EDGE,"E9.4.1.11"),sQuery(id+"F0.wireOp",EDGE,"E9.4.1.12"),sQuery(id+"F0.wireOp",EDGE,"E9.4.1.13"),sQuery(id+"F0.wireOp",EDGE,"E9.4.1.14"),sQuery(id+"F0.wireOp",EDGE,"E9.4.1.15"),sQuery(id+"F0.wireOp",EDGE,"E9.4.1.16"),sQuery(id+"F0.wireOp",EDGE,"E9.4.1.17"),sQuery(id+"F0.wireOp",EDGE,"E9.4.1.18"),sQuery(id+"F0.wireOp",EDGE,"E9.4.1.19"),sQuery(id+"F0.wireOp",EDGE,"E9.4.2.0"),sQuery(id+"F0.wireOp",EDGE,"E9.4.2.1"),sQuery(id+"F0.wireOp",EDGE,"E9.4.2.2"),sQuery(id+"F0.wireOp",EDGE,"E9.4.2.3"),sQuery(id+"F0.wireOp",EDGE,"E9.4.2.4"),sQuery(id+"F0.wireOp",EDGE,"E9.4.2.5"),sQuery(id+"F0.wireOp",EDGE,"E9.4.2.6"),sQuery(id+"F0.wireOp",EDGE,"E9.4.2.7"),sQuery(id+"F0.wireOp",EDGE,"E9.4.2.8"),sQuery(id+"F0.wireOp",EDGE,"E9.4.2.9"),sQuery(id+"F0.wireOp",EDGE,"E9.4.2.10"),sQuery(id+"F0.wireOp",EDGE,"E9.4.2.11"),sQuery(id+"F0.wireOp",EDGE,"E9.4.2.12"),sQuery(id+"F0.wireOp",EDGE,"E9.4.2.13"),sQuery(id+"F0.wireOp",EDGE,"E9.4.2.14"),sQuery(id+"F0.wireOp",EDGE,"E9.4.2.15"),sQuery(id+"F0.wireOp",EDGE,"E9.4.2.16"),sQuery(id+"F0.wireOp",EDGE,"E9.4.2.17"),sQuery(id+"F0.wireOp",EDGE,"E9.4.2.18"),sQuery(id+"F0.wireOp",EDGE,"E9.4.2.19"),sQuery(id+"F0.wireOp",EDGE,"E9.4.3.0"),sQuery(id+"F0.wireOp",EDGE,"E9.4.3.1"),sQuery(id+"F0.wireOp",EDGE,"E9.4.3.2"),sQuery(id+"F0.wireOp",EDGE,"E9.4.3.3"),sQuery(id+"F0.wireOp",EDGE,"E9.4.3.4"),sQuery(id+"F0.wireOp",EDGE,"E9.4.3.5"),sQuery(id+"F0.wireOp",EDGE,"E9.4.3.6"),sQuery(id+"F0.wireOp",EDGE,"E9.4.3.7"),sQuery(id+"F0.wireOp",EDGE,"E9.4.3.8"),sQuery(id+"F0.wireOp",EDGE,"E9.4.3.9"),sQuery(id+"F0.wireOp",EDGE,"E9.4.3.10"),sQuery(id+"F0.wireOp",EDGE,"E9.4.3.11"),sQuery(id+"F0.wireOp",EDGE,"E9.4.3.12"),sQuery(id+"F0.wireOp",EDGE,"E9.4.3.13"),sQuery(id+"F0.wireOp",EDGE,"E9.4.3.14"),sQuery(id+"F0.wireOp",EDGE,"E9.4.3.15"),sQuery(id+"F0.wireOp",EDGE,"E9.4.3.16"),sQuery(id+"F0.wireOp",EDGE,"E9.4.3.17"),sQuery(id+"F0.wireOp",EDGE,"E9.4.3.18"),sQuery(id+"F0.wireOp",EDGE,"E9.4.3.19"),sQuery(id+"F0.wireOp",EDGE,"E9.5.0.0"),sQuery(id+"F0.wireOp",EDGE,"E9.5.0.1"),sQuery(id+"F0.wireOp",EDGE,"E9.5.0.2"),sQuery(id+"F0.wireOp",EDGE,"E9.5.0.3"),sQuery(id+"F0.wireOp",EDGE,"E9.5.0.4"),sQuery(id+"F0.wireOp",EDGE,"E9.5.0.5"),sQuery(id+"F0.wireOp",EDGE,"E9.5.0.6"),sQuery(id+"F0.wireOp",EDGE,"E9.5.0.7"),sQuery(id+"F0.wireOp",EDGE,"E9.5.0.8"),sQuery(id+"F0.wireOp",EDGE,"E9.5.0.9"),sQuery(id+"F0.wireOp",EDGE,"E9.5.0.10"),sQuery(id+"F0.wireOp",EDGE,"E9.5.0.11"),sQuery(id+"F0.wireOp",EDGE,"E9.5.0.12"),sQuery(id+"F0.wireOp",EDGE,"E9.5.0.13"),sQuery(id+"F0.wireOp",EDGE,"E9.5.0.14"),sQuery(id+"F0.wireOp",EDGE,"E9.5.0.15"),sQuery(id+"F0.wireOp",EDGE,"E9.5.0.16"),sQuery(id+"F0.wireOp",EDGE,"E9.5.0.17"),sQuery(id+"F0.wireOp",EDGE,"E9.5.0.18"),sQuery(id+"F0.wireOp",EDGE,"E9.5.0.19"),sQuery(id+"F0.wireOp",EDGE,"E9.5.1.0"),sQuery(id+"F0.wireOp",EDGE,"E9.5.1.1"),sQuery(id+"F0.wireOp",EDGE,"E9.5.1.2"),sQuery(id+"F0.wireOp",EDGE,"E9.5.1.3"),sQuery(id+"F0.wireOp",EDGE,"E9.5.1.4"),sQuery(id+"F0.wireOp",EDGE,"E9.5.1.5"),sQuery(id+"F0.wireOp",EDGE,"E9.5.1.6"),sQuery(id+"F0.wireOp",EDGE,"E9.5.1.7"),sQuery(id+"F0.wireOp",EDGE,"E9.5.1.8"),sQuery(id+"F0.wireOp",EDGE,"E9.5.1.9"),sQuery(id+"F0.wireOp",EDGE,"E9.5.1.10"),sQuery(id+"F0.wireOp",EDGE,"E9.5.1.11"),sQuery(id+"F0.wireOp",EDGE,"E9.5.1.12"),sQuery(id+"F0.wireOp",EDGE,"E9.5.1.13"),sQuery(id+"F0.wireOp",EDGE,"E9.5.1.14"),sQuery(id+"F0.wireOp",EDGE,"E9.5.1.15"),sQuery(id+"F0.wireOp",EDGE,"E9.5.1.16"),sQuery(id+"F0.wireOp",EDGE,"E9.5.1.17"),sQuery(id+"F0.wireOp",EDGE,"E9.5.1.18"),sQuery(id+"F0.wireOp",EDGE,"E9.5.1.19"),sQuery(id+"F0.wireOp",EDGE,"E9.5.2.0"),sQuery(id+"F0.wireOp",EDGE,"E9.5.2.1"),sQuery(id+"F0.wireOp",EDGE,"E9.5.2.2"),sQuery(id+"F0.wireOp",EDGE,"E9.5.2.3"),sQuery(id+"F0.wireOp",EDGE,"E9.5.2.4"),sQuery(id+"F0.wireOp",EDGE,"E9.5.2.5"),sQuery(id+"F0.wireOp",EDGE,"E9.5.2.6"),sQuery(id+"F0.wireOp",EDGE,"E9.5.2.7"),sQuery(id+"F0.wireOp",EDGE,"E9.5.2.8"),sQuery(id+"F0.wireOp",EDGE,"E9.5.2.9"),sQuery(id+"F0.wireOp",EDGE,"E9.5.2.10"),sQuery(id+"F0.wireOp",EDGE,"E9.5.2.11"),sQuery(id+"F0.wireOp",EDGE,"E9.5.2.12"),sQuery(id+"F0.wireOp",EDGE,"E9.5.2.13"),sQuery(id+"F0.wireOp",EDGE,"E9.5.2.14"),sQuery(id+"F0.wireOp",EDGE,"E9.5.2.15"),sQuery(id+"F0.wireOp",EDGE,"E9.5.2.16"),sQuery(id+"F0.wireOp",EDGE,"E9.5.2.17"),sQuery(id+"F0.wireOp",EDGE,"E9.5.2.18"),sQuery(id+"F0.wireOp",EDGE,"E9.5.2.19"),sQuery(id+"F0.wireOp",EDGE,"E9.5.3.0"),sQuery(id+"F0.wireOp",EDGE,"E9.5.3.1"),sQuery(id+"F0.wireOp",EDGE,"E9.5.3.2"),sQuery(id+"F0.wireOp",EDGE,"E9.5.3.3"),sQuery(id+"F0.wireOp",EDGE,"E9.5.3.4"),sQuery(id+"F0.wireOp",EDGE,"E9.5.3.5"),sQuery(id+"F0.wireOp",EDGE,"E9.5.3.6"),sQuery(id+"F0.wireOp",EDGE,"E9.5.3.7"),sQuery(id+"F0.wireOp",EDGE,"E9.5.3.8"),sQuery(id+"F0.wireOp",EDGE,"E9.5.3.9"),sQuery(id+"F0.wireOp",EDGE,"E9.5.3.10"),sQuery(id+"F0.wireOp",EDGE,"E9.5.3.11"),sQuery(id+"F0.wireOp",EDGE,"E9.5.3.12"),sQuery(id+"F0.wireOp",EDGE,"E9.5.3.13"),sQuery(id+"F0.wireOp",EDGE,"E9.5.3.14"),sQuery(id+"F0.wireOp",EDGE,"E9.5.3.15"),sQuery(id+"F0.wireOp",EDGE,"E9.5.3.16"),sQuery(id+"F0.wireOp",EDGE,"E9.5.3.17"),sQuery(id+"F0.wireOp",EDGE,"E9.5.3.18"),sQuery(id+"F0.wireOp",EDGE,"E9.5.3.19"),sQuery(id+"F0.wireOp",EDGE,"E10.bottom"),sQuery(id+"F0.wireOp",EDGE,"E10.top"),sQuery(id+"F0.wireOp",EDGE,"E10.left"),sQuery(id+"F0.wireOp",EDGE,"E10.right")])],"isStart":false});
            extrude(context, id + "F5", {"entities" : qUnion([Q0]), "operationType" : NewBodyOperationType.ADD, "endBound" : BoundingType.UP_TO_SURFACE, "endBoundEntityFace" : qUnion([Q1]), "depth" : 40 * mm});
        }
    });
